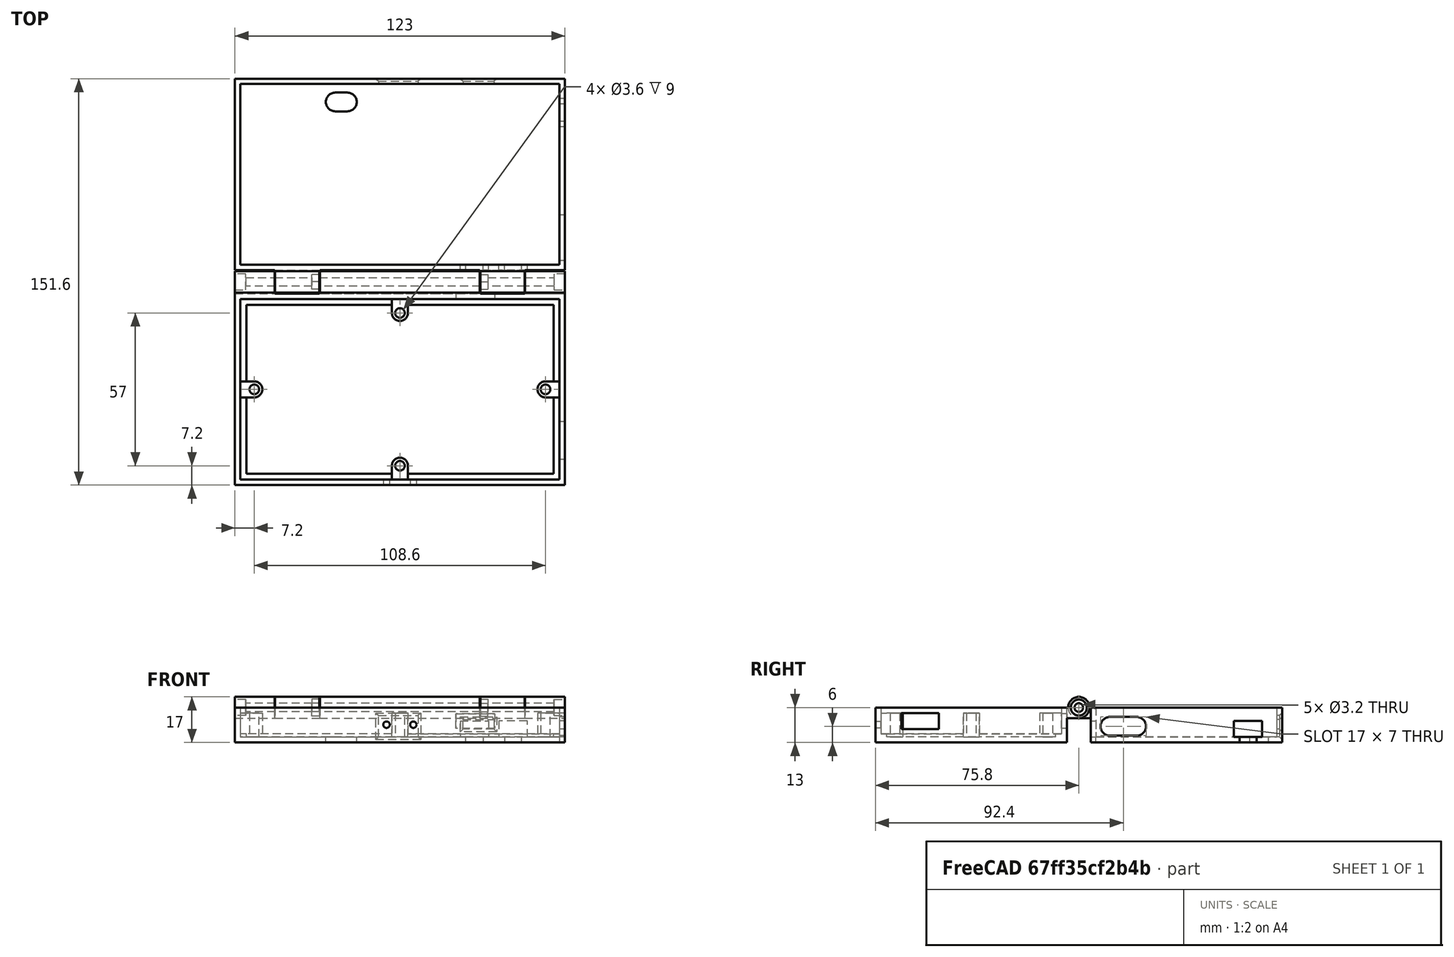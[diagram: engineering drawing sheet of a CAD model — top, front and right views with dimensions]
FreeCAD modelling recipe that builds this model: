
FCSTD DOCUMENT  (FreeCAD 1.0R39319 (Git))
Label: M3-MOD
License: All rights reserved
LicenseURL: http://en.wikipedia.org/wiki/All_rights_reserved
objects: Sketcher::SketchObject×31, PartDesign::Pocket×19, PartDesign::SubShapeBinder×12, PartDesign::Body×3, PartDesign::Pad×3, Mesh::Feature×2, PartDesign::Chamfer×1
note: 146 computed .brp shape members not serialized (recipe doc carries the construction recipe); baked Part::Feature solids carry a one-line shape summary decoded from their .brp

FEATURE [Sketcher::SketchObject] Sketch  label="Workspace"
  ArcFitTolerance = 0
  AttachmentSupport = -> [XY_Plane]
  FullyConstrained = true
  MakeInternals = false
  MapMode = 5
  sketch-geometry (24):
    g0: LineSegment StartX=-59.3 StartY=-6.6 StartZ=0 EndX=59.3 EndY=-6.6 EndZ=0
    g1: LineSegment StartX=59.3 StartY=-6.6 StartZ=0 EndX=59.3 EndY=-73.6 EndZ=0
    g2: LineSegment StartX=59.3 StartY=-73.6 StartZ=0 EndX=-59.3 EndY=-73.6 EndZ=0
    g3: LineSegment StartX=-59.3 StartY=-73.6 StartZ=0 EndX=-59.3 EndY=-6.6 EndZ=0
    g4: LineSegment StartX=-59.3 StartY=73.6 StartZ=0 EndX=59.3 EndY=73.6 EndZ=0
    g5: LineSegment StartX=59.3 StartY=73.6 StartZ=0 EndX=59.3 EndY=6.6 EndZ=0
    g6: LineSegment StartX=59.3 StartY=6.6 StartZ=0 EndX=-59.3 EndY=6.6 EndZ=0
    g7: LineSegment StartX=-59.3 StartY=6.6 StartZ=0 EndX=-59.3 EndY=73.6 EndZ=0
    g8: LineSegment StartX=-61.5 StartY=4 StartZ=0 EndX=-61.5 EndY=-4 EndZ=0
    g9: LineSegment StartX=-61.5 StartY=-4 StartZ=0 EndX=-46.5 EndY=-4 EndZ=0
    g10: LineSegment StartX=-46.5 StartY=-4 StartZ=0 EndX=-46.5 EndY=4 EndZ=0
    g11: LineSegment StartX=-46.5 StartY=4 StartZ=0 EndX=-61.5 EndY=4 EndZ=0
    g12: LineSegment StartX=-30 StartY=4 StartZ=0 EndX=-30 EndY=-4 EndZ=0
    g13: LineSegment StartX=-30 StartY=-4 StartZ=0 EndX=30 EndY=-4 EndZ=0
    g14: LineSegment StartX=30 StartY=-4 StartZ=0 EndX=30 EndY=4 EndZ=0
    g15: LineSegment StartX=30 StartY=4 StartZ=0 EndX=-30 EndY=4 EndZ=0
    g16: LineSegment StartX=61.5 StartY=4 StartZ=0 EndX=46.5 EndY=4 EndZ=0
    g17: LineSegment StartX=46.5 StartY=4 StartZ=0 EndX=46.5 EndY=-4 EndZ=0
    g18: LineSegment StartX=46.5 StartY=-4 StartZ=0 EndX=61.5 EndY=-4 EndZ=0
    g19: LineSegment StartX=61.5 StartY=-4 StartZ=0 EndX=61.5 EndY=4 EndZ=0
    g20: LineSegment StartX=-61.5 StartY=75.8 StartZ=0 EndX=-61.5 EndY=-75.8 EndZ=0
    g21: LineSegment StartX=-61.5 StartY=-75.8 StartZ=0 EndX=61.5 EndY=-75.8 EndZ=0
    g22: LineSegment StartX=61.5 StartY=-75.8 StartZ=0 EndX=61.5 EndY=75.8 EndZ=0
    g23: LineSegment StartX=61.5 StartY=75.8 StartZ=0 EndX=-61.5 EndY=75.8 EndZ=0
  constraints (68):
    c: Coincident(g0,g1)
    c: Coincident(g1,g2)
    c: Coincident(g2,g3)
    c: Coincident(g3,g0)
    c: Horizontal(g2)
    c: Vertical(g1)
    c: Vertical(g3)
    c: Symmetric(g0,g0,g-2)
    c: DistanceY(g1,g1) = 67
    c: DistanceY(g0,g-1) = 6.6
    c: Coincident(g4,g5)
    c: Coincident(g5,g6)
    c: Coincident(g6,g7)
    c: Coincident(g7,g4)
    c: Horizontal(g6)
    c: Vertical(g5)
    c: Vertical(g7)
    c: Equal(g0,g6)
    c: Equal(g1,g5)
    c: DistanceX(g2,g2) = 118.6
    c: DistanceY(g-1,g5) = 6.6
    c: Symmetric(g4,g4,g-2)
    c: Coincident(g8,g9)
    c: Coincident(g9,g10)
    c: Coincident(g10,g11)
    c: Coincident(g11,g8)
    c: Vertical(g10)
    c: Horizontal(g9)
    c: Horizontal(g11)
    c: Coincident(g12,g13)
    c: Coincident(g13,g14)
    c: Coincident(g14,g15)
    c: Coincident(g15,g12)
    c: Vertical(g12)
    c: Vertical(g14)
    c: Horizontal(g13)
    c: Coincident(g16,g17)
    c: Coincident(g17,g18)
    c: Coincident(g18,g19)
    c: Coincident(g19,g16)
    c: Horizontal(g16)
    c: Horizontal(g18)
    c: Vertical(g17)
    c: Vertical(g19)
    c: Coincident(g20,g21)
    c: Coincident(g21,g22)
    c: Coincident(g22,g23)
    c: Coincident(g23,g20)
    c: Vertical(g20)
    c: Vertical(g22)
    c: Horizontal(g21)
    c: Horizontal(g23)
    c: DistanceX(g20,g2) = 2.2
    c: DistanceX(g1,g21) = 2.2
    c: DistanceY(g20,g2) = 2.2
    c: DistanceY(g4,g20) = 2.2
    c: Equal(g10,g14)
    c: Equal(g14,g17)
    c: DistanceY(g19,g19) = 8
    c: Symmetric(g8,g8,g-1)
    c: Horizontal(g10,g12)
    c: Horizontal(g16,g14)
    c: Symmetric(g12,g14,g-2)
    c: Vertical(g20,g8)
    c: Vertical(g16,g22)
    c: Equal(g11,g16)
    c: DistanceX(g9,g9) = 15
    c: DistanceX(g13,g13) = 60
FEATURE [Sketcher::SketchObject] Sketch022  label="Key & SD"
  ArcFitTolerance = 0
  AttachmentOffset = pos=(0,0,-75.2) rot=(0,0,1;0rad)
  AttachmentSupport = -> [XZ_Plane]
  FullyConstrained = true
  MakeInternals = false
  MapMode = 5
  Placement = pos=(0,75.2,-1.67e-14) rot=(1,0,0;1.5708rad)
  sketch-geometry (8):
    g0: LineSegment StartX=23.5 StartY=-4.5 StartZ=0 EndX=35.1 EndY=-4.5 EndZ=0
    g1: LineSegment StartX=35.1 StartY=-4.5 StartZ=0 EndX=35.1 EndY=-8 EndZ=0
    g2: LineSegment StartX=35.1 StartY=-8 StartZ=0 EndX=23.5 EndY=-8 EndZ=0
    g3: LineSegment StartX=23.5 StartY=-8 StartZ=0 EndX=23.5 EndY=-4.5 EndZ=0
    g4: LineSegment StartX=-8 StartY=-3 StartZ=0 EndX=6.8 EndY=-3 EndZ=0
    g5: LineSegment StartX=6.8 StartY=-3 StartZ=0 EndX=6.8 EndY=-11 EndZ=0
    g6: LineSegment StartX=6.8 StartY=-11 StartZ=0 EndX=-8 EndY=-11 EndZ=0
    g7: LineSegment StartX=-8 StartY=-11 StartZ=0 EndX=-8 EndY=-3 EndZ=0
  constraints (24):
    c: Coincident(g0,g1)
    c: Coincident(g1,g2)
    c: Coincident(g2,g3)
    c: Coincident(g3,g0)
    c: Horizontal(g0)
    c: Horizontal(g2)
    c: Vertical(g1)
    c: Vertical(g3)
    c: Coincident(g4,g5)
    c: Coincident(g5,g6)
    c: Coincident(g6,g7)
    c: Coincident(g7,g4)
    c: Horizontal(g4)
    c: Horizontal(g6)
    c: Vertical(g5)
    c: Vertical(g7)
    c: DistanceX(g0,g0) = 11.6
    c: DistanceX(g4,g4) = 14.8
    c: DistanceY(g7,g7) = 8
    c: DistanceY(g1,g1) = 3.5
    c: DistanceX(g-1,g1) = 35.1
    c: DistanceX(g-1,g5) = 6.8
    c: DistanceY(g1,g-1) = 8
    c: DistanceY(g6,g-1) = 11
FEATURE [Sketcher::SketchObject] Sketch023  label="USB & CONN"
  ArcFitTolerance = 0
  AttachmentOffset = pos=(0,0,61.5) rot=(0,0,1;0rad)
  AttachmentSupport = -> [YZ_Plane]
  ExternalGeometry = -> [Sketch]
  FullyConstrained = true
  MakeInternals = false
  MapMode = 5
  Placement = pos=(61.5,0,0) rot=(0.57735,0.57735,0.57735;2.0944rad)
  sketch-geometry (12):
    g0: ArcOfCircle CenterX=11.6 CenterY=-7 CenterZ=0 NormalX=0 NormalY=0 NormalZ=1 AngleXU=0 Radius=3.5 StartAngle=1.5708 EndAngle=4.71239
    g1: ArcOfCircle CenterX=21.6 CenterY=-7 CenterZ=0 NormalX=0 NormalY=0 NormalZ=1 AngleXU=0 Radius=3.5 StartAngle=4.71239 EndAngle=7.85398
    g2: LineSegment StartX=11.6 StartY=-10.5 StartZ=0 EndX=21.6 EndY=-10.5 EndZ=0
    g3: LineSegment StartX=11.6 StartY=-3.5 StartZ=0 EndX=21.6 EndY=-3.5 EndZ=0
    g4: LineSegment StartX=57.8 StartY=-5 StartZ=0 EndX=68.4 EndY=-5 EndZ=0
    g5: LineSegment StartX=68.4 StartY=-5 StartZ=0 EndX=68.4 EndY=-11 EndZ=0
    g6: LineSegment StartX=68.4 StartY=-11 StartZ=0 EndX=66.3 EndY=-11 EndZ=0
    g7: LineSegment StartX=57.8 StartY=-11 StartZ=0 EndX=57.8 EndY=-5 EndZ=0
    g8: LineSegment StartX=66.3 StartY=-11 StartZ=0 EndX=66.3 EndY=-13 EndZ=0
    g9: LineSegment StartX=66.3 StartY=-13 StartZ=0 EndX=59.9 EndY=-13 EndZ=0
    g10: LineSegment StartX=59.9 StartY=-13 StartZ=0 EndX=59.9 EndY=-11 EndZ=0
    g11: LineSegment StartX=59.9 StartY=-11 StartZ=0 EndX=57.8 EndY=-11 EndZ=0
  constraints (33):
    c: Tangent(g0,g3) = 1.5708
    c: Tangent(g0,g2) = -1.5708
    c: Tangent(g2,g1) = -1.5708
    c: Tangent(g3,g1) = 1.5708
    c: Horizontal(g2)
    c: Equal(g0,g1)
    c: Coincident(g4,g5)
    c: Coincident(g5,g6)
    c: Coincident(g11,g7)
    c: Coincident(g7,g4)
    c: Horizontal(g4)
    c: Horizontal(g6)
    c: Vertical(g5)
    c: Vertical(g7)
    c: Coincident(g8,g9)
    c: Coincident(g9,g10)
    c: Horizontal(g9)
    c: Vertical(g8)
    c: Vertical(g10)
    c: Coincident(g6,g8)
    c: Coincident(g11,g10)
    c: Tangent(g6,g11)
    c: Equal(g6,g11)
    c: DistanceX(g9,g9) = 6.4
    c: DistanceX(g4,g4) = 10.6
    c: DistanceY(g5,g5) = 6
    c: DistanceY(g8,g5) = 2
    c: Radius(g1) = 3.5
    c: DistanceX(g0,g1) = 10
    c: DistanceY(g8,g-3) = 13
    c: DistanceX(g4,g-3) = 5.2
    c: DistanceY(g0,g-3) = 7
    c: DistanceX(g-3,g0) = 5
FEATURE [Sketcher::SketchObject] Sketch024  label="CONN 2"
  ArcFitTolerance = 0
  AttachmentOffset = pos=(0,0,-4.2) rot=(0,0,1;0rad)
  AttachmentSupport = -> [XZ_Plane]
  ExternalGeometry = -> [Sketch]
  FullyConstrained = true
  MakeInternals = false
  MapMode = 5
  Placement = pos=(0,4.2,-9e-16) rot=(1,0,0;1.5708rad)
  sketch-geometry (16):
    g0: LineSegment StartX=22.5 StartY=-5 StartZ=0 EndX=33.1 EndY=-5 EndZ=0
    g1: LineSegment StartX=33.1 StartY=-5 StartZ=0 EndX=33.1 EndY=-11 EndZ=0
    g2: LineSegment StartX=33.1 StartY=-11 StartZ=0 EndX=31 EndY=-11 EndZ=0
    g3: LineSegment StartX=22.5 StartY=-11 StartZ=0 EndX=22.5 EndY=-5 EndZ=0
    g4: LineSegment StartX=31 StartY=-11 StartZ=0 EndX=31 EndY=-13 EndZ=0
    g5: LineSegment StartX=31 StartY=-13 StartZ=0 EndX=24.6 EndY=-13 EndZ=0
    g6: LineSegment StartX=24.6 StartY=-13 StartZ=0 EndX=24.6 EndY=-11 EndZ=0
    g7: LineSegment StartX=36.9 StartY=-5 StartZ=0 EndX=47.5 EndY=-5 EndZ=0
    g8: LineSegment StartX=47.5 StartY=-5 StartZ=0 EndX=47.5 EndY=-11 EndZ=0
    g9: LineSegment StartX=47.5 StartY=-11 StartZ=0 EndX=45.4 EndY=-11 EndZ=0
    g10: LineSegment StartX=36.9 StartY=-11 StartZ=0 EndX=36.9 EndY=-5 EndZ=0
    g11: LineSegment StartX=45.4 StartY=-11 StartZ=0 EndX=45.4 EndY=-13 EndZ=0
    g12: LineSegment StartX=45.4 StartY=-13 StartZ=0 EndX=39 EndY=-13 EndZ=0
    g13: LineSegment StartX=39 StartY=-13 StartZ=0 EndX=39 EndY=-11 EndZ=0
    g14: LineSegment StartX=24.6 StartY=-11 StartZ=0 EndX=22.5 EndY=-11 EndZ=0
    g15: LineSegment StartX=39 StartY=-11 StartZ=0 EndX=36.9 EndY=-11 EndZ=0
  constraints (46):
    c: Coincident(g0,g1)
    c: Coincident(g1,g2)
    c: Coincident(g14,g3)
    c: Coincident(g3,g0)
    c: Horizontal(g0)
    c: Horizontal(g2)
    c: Vertical(g1)
    c: Vertical(g3)
    c: Coincident(g4,g5)
    c: Coincident(g5,g6)
    c: Horizontal(g5)
    c: Vertical(g4)
    c: Vertical(g6)
    c: Coincident(g7,g8)
    c: Coincident(g8,g9)
    c: Coincident(g15,g10)
    c: Coincident(g10,g7)
    c: Horizontal(g7)
    c: Horizontal(g9)
    c: Vertical(g8)
    c: Vertical(g10)
    c: Coincident(g11,g12)
    c: Coincident(g12,g13)
    c: Horizontal(g12)
    c: Vertical(g11)
    c: Vertical(g13)
    c: Coincident(g2,g4)
    c: Coincident(g14,g6)
    c: Tangent(g2,g14)
    c: Coincident(g9,g11)
    c: Coincident(g15,g13)
    c: Tangent(g9,g15)
    c: Equal(g14,g2)
    c: Equal(g2,g15)
    c: Equal(g15,g9)
    c: Equal(g1,g10)
    c: Equal(g0,g7)
    c: Horizontal(g4,g12)
    c: Horizontal(g1,g10)
    c: DistanceY(g11,g8) = 2
    c: DistanceX(g7,g7) = 10.6
    c: DistanceY(g8,g8) = 6
    c: DistanceX(g12,g12) = 6.4
    c: DistanceY(g11,g-1) = 13
    c: DistanceX(g7,g-3) = 11.8
    c: DistanceX(g0,g-3) = 26.2
FEATURE [Sketcher::SketchObject] Sketch025  label="RESET"
  ArcFitTolerance = 0
  AttachmentSupport = -> [XY_Plane]
  ExternalGeometry = -> [Sketch]
  FullyConstrained = true
  MakeInternals = false
  MapMode = 5
  sketch-geometry (4):
    g0: ArcOfCircle CenterX=-24.1 CenterY=67.1 CenterZ=0 NormalX=0 NormalY=0 NormalZ=1 AngleXU=0 Radius=3.5 StartAngle=1.5708 EndAngle=4.71239
    g1: ArcOfCircle CenterX=-19.6 CenterY=67.1 CenterZ=0 NormalX=0 NormalY=0 NormalZ=1 AngleXU=0 Radius=3.5 StartAngle=4.71239 EndAngle=7.85398
    g2: LineSegment StartX=-24.1 StartY=63.6 StartZ=0 EndX=-19.6 EndY=63.6 EndZ=0
    g3: LineSegment StartX=-24.1 StartY=70.6 StartZ=0 EndX=-19.6 EndY=70.6 EndZ=0
  constraints (10):
    c: Tangent(g0,g3) = 1.5708
    c: Tangent(g0,g2) = -1.5708
    c: Tangent(g2,g1) = -1.5708
    c: Tangent(g3,g1) = 1.5708
    c: Horizontal(g2)
    c: Equal(g0,g1)
    c: Radius(g0) = 3.5
    c: DistanceX(g0,g1) = 4.5
    c: DistanceX(g-3,g0) = 35.2
    c: DistanceY(g0,g-4) = 3
FEATURE [Sketcher::SketchObject] Sketch031  label="FIX HOLE"
  ArcFitTolerance = 0
  AttachmentSupport = -> [XY_Plane]
  ExternalGeometry = -> [Sketch]
  FullyConstrained = true
  MakeInternals = false
  MapMode = 5
  sketch-geometry (32):
    g0: LineSegment StartX=-3 StartY=-8.6 StartZ=0 EndX=3 EndY=-8.6 EndZ=0
    g1: LineSegment StartX=3 StartY=-8.6 StartZ=0 EndX=3 EndY=-11.6 EndZ=0
    g2: LineSegment StartX=2.02025e-10 StartY=-14.6 StartZ=0 EndX=-2.01994e-10 EndY=-14.6 EndZ=0
    g3: LineSegment StartX=-3 StartY=-11.6 StartZ=0 EndX=-3 EndY=-8.6 EndZ=0
    g4: LineSegment StartX=54.3 StartY=-37.1 StartZ=0 EndX=57.3 EndY=-37.1 EndZ=0
    g5: LineSegment StartX=57.3 StartY=-37.1 StartZ=0 EndX=57.3 EndY=-43.1 EndZ=0
    g6: LineSegment StartX=57.3 StartY=-43.1 StartZ=0 EndX=54.3 EndY=-43.1 EndZ=0
    g7: LineSegment StartX=51.3 StartY=-40.1 StartZ=0 EndX=51.3 EndY=-40.1 EndZ=0
    g8: LineSegment StartX=-2.04292e-10 StartY=-65.6 StartZ=0 EndX=2.04323e-10 EndY=-65.6 EndZ=0
    g9: LineSegment StartX=3 StartY=-68.6 StartZ=0 EndX=3 EndY=-71.6 EndZ=0
    g10: LineSegment StartX=3 StartY=-71.6 StartZ=0 EndX=-3 EndY=-71.6 EndZ=0
    g11: LineSegment StartX=-3 StartY=-71.6 StartZ=0 EndX=-3 EndY=-68.6 EndZ=0
    g12: LineSegment StartX=-57.3 StartY=-37.1 StartZ=0 EndX=-54.3 EndY=-37.1 EndZ=0
    g13: LineSegment StartX=-51.3 StartY=-40.1 StartZ=0 EndX=-51.3 EndY=-40.1 EndZ=0
    g14: LineSegment StartX=-54.3 StartY=-43.1 StartZ=0 EndX=-57.3 EndY=-43.1 EndZ=0
    g15: LineSegment StartX=-57.3 StartY=-43.1 StartZ=0 EndX=-57.3 EndY=-37.1 EndZ=0
    g16: ArcOfCircle CenterX=-54.3 CenterY=-40.1 CenterZ=0 NormalX=0 NormalY=0 NormalZ=1 AngleXU=0 Radius=3 StartAngle=5.39571e-11 EndAngle=1.5708
    g17: ArcOfCircle CenterX=-54.3 CenterY=-40.1 CenterZ=0 NormalX=0 NormalY=0 NormalZ=1 AngleXU=0 Radius=3 StartAngle=4.71239 EndAngle=6.28319
    g18: ArcOfCircle CenterX=-4.11221e-11 CenterY=-11.6 CenterZ=0 NormalX=0 NormalY=0 NormalZ=1 AngleXU=0 Radius=3 StartAngle=3.14159 EndAngle=4.71239
    g19: ArcOfCircle CenterX=4.12844e-11 CenterY=-11.6 CenterZ=0 NormalX=0 NormalY=0 NormalZ=1 AngleXU=0 Radius=3 StartAngle=4.71239 EndAngle=6.28319
    g20: ArcOfCircle CenterX=-4.0526e-11 CenterY=-68.6 CenterZ=0 NormalX=0 NormalY=0 NormalZ=1 AngleXU=0 Radius=3 StartAngle=1.5708 EndAngle=3.14159
    g21: ArcOfCircle CenterX=4.0686e-11 CenterY=-68.6 CenterZ=0 NormalX=0 NormalY=0 NormalZ=1 AngleXU=0 Radius=3 StartAngle=5.62494e-11 EndAngle=1.5708
    g22: ArcOfCircle CenterX=54.3 CenterY=-40.1 CenterZ=0 NormalX=0 NormalY=0 NormalZ=1 AngleXU=0 Radius=3 StartAngle=1.5708 EndAngle=3.14159
    g23: ArcOfCircle CenterX=54.3 CenterY=-40.1 CenterZ=0 NormalX=0 NormalY=0 NormalZ=1 AngleXU=0 Radius=3 StartAngle=3.14159 EndAngle=4.71239
    g24: LineSegment [constr] StartX=57.3 StartY=-8.6 StartZ=0 EndX=57.3 EndY=-37.1 EndZ=0
    g25: LineSegment [constr] StartX=57.3 StartY=-71.6 StartZ=0 EndX=57.3 EndY=-43.1 EndZ=0
    g26: LineSegment [constr] StartX=-57.3 StartY=-71.6 StartZ=0 EndX=-3 EndY=-71.6 EndZ=0
    g27: LineSegment [constr] StartX=3 StartY=-71.6 StartZ=0 EndX=57.3 EndY=-71.6 EndZ=0
    g28: LineSegment [constr] StartX=-57.3 StartY=-71.6 StartZ=0 EndX=-57.3 EndY=-43.1 EndZ=0
    g29: LineSegment [constr] StartX=-57.3 StartY=-37.1 StartZ=0 EndX=-57.3 EndY=-8.6 EndZ=0
    g30: LineSegment [constr] StartX=-57.3 StartY=-8.6 StartZ=0 EndX=-3 EndY=-8.6 EndZ=0
    g31: LineSegment [constr] StartX=3 StartY=-8.6 StartZ=0 EndX=57.3 EndY=-8.6 EndZ=0
  constraints (84):
    c: Coincident(g0,g1)
    c: Coincident(g3,g0)
    c: Horizontal(g0)
    c: Horizontal(g2)
    c: Vertical(g1)
    c: Vertical(g3)
    c: Coincident(g4,g5)
    c: Coincident(g5,g6)
    c: Horizontal(g4)
    c: Horizontal(g6)
    c: Vertical(g5)
    c: Vertical(g7)
    c: Coincident(g9,g10)
    c: Coincident(g10,g11)
    c: Horizontal(g8)
    c: Horizontal(g10)
    c: Vertical(g9)
    c: Vertical(g11)
    c: Coincident(g14,g15)
    c: Coincident(g15,g12)
    c: Horizontal(g12)
    c: Horizontal(g14)
    c: Vertical(g13)
    c: Vertical(g15)
    c: Tangent(g12,g16) = 1.5708
    c: Tangent(g13,g16) = 1.5708
    c: Tangent(g13,g17) = 1.5708
    c: Tangent(g14,g17) = 1.5708
    c: Tangent(g2,g18) = 1.5708
    c: Tangent(g3,g18) = 1.5708
    c: Tangent(g1,g19) = 1.5708
    c: Tangent(g2,g19) = 1.5708
    c: Tangent(g8,g20) = 1.5708
    c: Tangent(g11,g20) = 1.5708
    c: Tangent(g8,g21) = 1.5708
    c: Tangent(g9,g21) = 1.5708
    c: Tangent(g4,g22) = 1.5708
    c: Tangent(g7,g22) = 1.5708
    c: Tangent(g6,g23) = 1.5708
    c: Tangent(g7,g23) = 1.5708
    c: Equal(g16,g17)
    c: Equal(g17,g18)
    c: Equal(g18,g19)
    c: Equal(g19,g20)
    c: Equal(g20,g21)
    c: Equal(g21,g23)
    c: Equal(g23,g22)
    c: Equal(g0,g5)
    c: Equal(g5,g10)
    c: Equal(g10,g15)
    c: Equal(g12,g1)
    c: Equal(g1,g6)
    c: Equal(g6,g11)
    c: DistanceX(g10,g10) = 6
    c: DistanceX(g25,g-5) = 2
    c: DistanceY(g-5,g25) = 2
    c: Coincident(g24,g4)
    c: Vertical(g24)
    c: Coincident(g25,g5)
    c: Vertical(g25)
    c: Equal(g24,g25)
    c: DistanceX(g-3,g29) = 2
    c: DistanceY(g29,g-3) = 2
    c: Coincident(g26,g10)
    c: Horizontal(g26)
    c: Coincident(g27,g9)
    c: Coincident(g27,g25)
    c: Horizontal(g27)
    c: Coincident(g28,g26)
    c: Coincident(g28,g14)
    c: Coincident(g29,g12)
    c: Coincident(g30,g29)
    c: Coincident(g30,g0)
    c: Coincident(g31,g0)
    c: Coincident(g31,g24)
    c: Horizontal(g31)
    c: Horizontal(g30)
    c: Vertical(g29)
    c: Vertical(g28)
    c: Equal(g28,g29)
    c: Equal(g30,g31)
    c: Equal(g26,g27)
    c: Radius(g21) = 3
    c: DistanceY(g9,g9) = 3
FEATURE [Sketcher::SketchObject] Sketch032  label="PARTS"
  ArcFitTolerance = 0
  AttachmentSupport = -> [XY_Plane]
  ExternalGeometry = -> [Sketch]
  FullyConstrained = true
  MakeInternals = false
  MapMode = 5
  sketch-geometry (44):
    g0: LineSegment StartX=6.9 StartY=-59.2 StartZ=0 EndX=22.3 EndY=-59.2 EndZ=0
    g1: LineSegment StartX=22.3 StartY=-59.2 StartZ=0 EndX=22.3 EndY=-71.2 EndZ=0
    g2: LineSegment StartX=22.3 StartY=-71.2 StartZ=0 EndX=6.9 EndY=-71.2 EndZ=0
    g3: LineSegment StartX=6.9 StartY=-71.2 StartZ=0 EndX=6.9 EndY=-59.2 EndZ=0
    g4: LineSegment StartX=-56.3 StartY=-9.4 StartZ=0 EndX=-36.3 EndY=-9.4 EndZ=0
    g5: LineSegment StartX=-36.3 StartY=-9.4 StartZ=0 EndX=-36.3 EndY=-23.4 EndZ=0
    g6: LineSegment StartX=-36.3 StartY=-23.4 StartZ=0 EndX=-56.3 EndY=-23.4 EndZ=0
    g7: LineSegment StartX=-56.3 StartY=-23.4 StartZ=0 EndX=-56.3 EndY=-9.4 EndZ=0
    g8: LineSegment StartX=-58.1 StartY=-46.6 StartZ=0 EndX=-32.1 EndY=-46.6 EndZ=0
    g9: LineSegment StartX=-32.1 StartY=-46.6 StartZ=0 EndX=-32.1 EndY=-72.6 EndZ=0
    g10: LineSegment StartX=-32.1 StartY=-72.6 StartZ=0 EndX=-58.1 EndY=-72.6 EndZ=0
    g11: LineSegment StartX=-58.1 StartY=-72.6 StartZ=0 EndX=-58.1 EndY=-46.6 EndZ=0
    g12: LineSegment StartX=43.9 StartY=-8.5 StartZ=0 EndX=58.9 EndY=-8.5 EndZ=0
    g13: LineSegment StartX=58.9 StartY=-8.5 StartZ=0 EndX=58.9 EndY=-32 EndZ=0
    g14: LineSegment StartX=58.9 StartY=-32 StartZ=0 EndX=43.9 EndY=-32 EndZ=0
    g15: LineSegment StartX=43.9 StartY=-32 StartZ=0 EndX=43.9 EndY=-8.5 EndZ=0
    g16: LineSegment StartX=24.3 StartY=-47.2 StartZ=0 EndX=58.3 EndY=-47.2 EndZ=0
    g17: LineSegment StartX=58.3 StartY=-47.2 StartZ=0 EndX=58.3 EndY=-72.6 EndZ=0
    g18: LineSegment StartX=58.3 StartY=-72.6 StartZ=0 EndX=24.3 EndY=-72.6 EndZ=0
    g19: LineSegment StartX=24.3 StartY=-72.6 StartZ=0 EndX=24.3 EndY=-47.2 EndZ=0
    g20: LineSegment StartX=-59.3 StartY=-6.6 StartZ=0 EndX=59.3 EndY=-6.6 EndZ=0
    g21: LineSegment StartX=59.3 StartY=-6.6 StartZ=0 EndX=59.3 EndY=-73.6 EndZ=0
    g22: LineSegment StartX=59.3 StartY=-73.6 StartZ=0 EndX=-59.3 EndY=-73.6 EndZ=0
    g23: LineSegment StartX=-59.3 StartY=-73.6 StartZ=0 EndX=-59.3 EndY=-6.6 EndZ=0
    g24: LineSegment StartX=21.9 StartY=-10.6 StartZ=0 EndX=34.3 EndY=-10.6 EndZ=0
    g25: LineSegment StartX=34.3 StartY=-10.6 StartZ=0 EndX=34.3 EndY=-18.6 EndZ=0
    g26: LineSegment StartX=34.3 StartY=-18.6 StartZ=0 EndX=21.9 EndY=-18.6 EndZ=0
    g27: LineSegment StartX=21.9 StartY=-18.6 StartZ=0 EndX=21.9 EndY=-10.6 EndZ=0
    g28: LineSegment StartX=2.2 StartY=-22.9 StartZ=0 EndX=-2.2 EndY=-22.9 EndZ=0
    g29: LineSegment StartX=-2.2 StartY=-22.9 StartZ=0 EndX=-2.2 EndY=-27.3 EndZ=0
    g30: LineSegment StartX=-2.2 StartY=-27.3 StartZ=0 EndX=2.2 EndY=-27.3 EndZ=0
    g31: LineSegment StartX=2.2 StartY=-27.3 StartZ=0 EndX=2.2 EndY=-22.9 EndZ=0
    g32: LineSegment StartX=-14.9 StartY=-35.6 StartZ=0 EndX=-10.5 EndY=-35.6 EndZ=0
    g33: LineSegment StartX=-10.5 StartY=-35.6 StartZ=0 EndX=-10.5 EndY=-40 EndZ=0
    g34: LineSegment StartX=-10.5 StartY=-40 StartZ=0 EndX=-14.9 EndY=-40 EndZ=0
    g35: LineSegment StartX=-14.9 StartY=-40 StartZ=0 EndX=-14.9 EndY=-35.6 EndZ=0
    g36: LineSegment StartX=10.5 StartY=-35.6 StartZ=0 EndX=14.9 EndY=-35.6 EndZ=0
    g37: LineSegment StartX=14.9 StartY=-35.6 StartZ=0 EndX=14.9 EndY=-40 EndZ=0
    g38: LineSegment StartX=14.9 StartY=-40 StartZ=0 EndX=10.5 EndY=-40 EndZ=0
    g39: LineSegment StartX=10.5 StartY=-40 StartZ=0 EndX=10.5 EndY=-35.6 EndZ=0
    g40: LineSegment StartX=-2.2 StartY=-48.7 StartZ=0 EndX=2.2 EndY=-48.7 EndZ=0
    g41: LineSegment StartX=2.2 StartY=-48.7 StartZ=0 EndX=2.2 EndY=-53.1 EndZ=0
    g42: LineSegment StartX=2.2 StartY=-53.1 StartZ=0 EndX=-2.2 EndY=-53.1 EndZ=0
    g43: LineSegment StartX=-2.2 StartY=-53.1 StartZ=0 EndX=-2.2 EndY=-48.7 EndZ=0
  constraints (128):
    c: Coincident(g0,g1)
    c: Coincident(g1,g2)
    c: Coincident(g2,g3)
    c: Coincident(g3,g0)
    c: Horizontal(g0)
    c: Horizontal(g2)
    c: Vertical(g1)
    c: Vertical(g3)
    c: Coincident(g4,g5)
    c: Coincident(g5,g6)
    c: Coincident(g6,g7)
    c: Coincident(g7,g4)
    c: Horizontal(g4)
    c: Horizontal(g6)
    c: Vertical(g5)
    c: Vertical(g7)
    c: Coincident(g8,g9)
    c: Coincident(g9,g10)
    c: Coincident(g10,g11)
    c: Coincident(g11,g8)
    c: Horizontal(g8)
    c: Horizontal(g10)
    c: Vertical(g9)
    c: Vertical(g11)
    c: Coincident(g12,g13)
    c: Coincident(g13,g14)
    c: Coincident(g14,g15)
    c: Coincident(g15,g12)
    c: Horizontal(g12)
    c: Horizontal(g14)
    c: Vertical(g13)
    c: Vertical(g15)
    c: Coincident(g16,g17)
    c: Coincident(g18,g19)
    c: Coincident(g19,g16)
    c: Horizontal(g16)
    c: Horizontal(g18)
    c: Vertical(g17)
    c: Vertical(g19)
    c: Coincident(g20,g21)
    c: Coincident(g21,g22)
    c: Coincident(g22,g23)
    c: Coincident(g23,g20)
    c: Horizontal(g20)
    c: Horizontal(g22)
    c: Vertical(g21)
    c: Vertical(g23)
    c: DistanceY(g18,g17) = 25.4
    c: DistanceX(g18,g18) = 34
    c: Equal(g10,g11)
    c: DistanceX(g10,g10) = 26
    c: DistanceY(g13,g13) = 23.5
    c: DistanceX(g12,g12) = 15
    c: DistanceX(g4,g4) = 20
    c: DistanceY(g7,g7) = 14
    c: DistanceY(g3,g3) = 12
    c: Coincident(g20,g-3)
    c: Coincident(g21,g-4)
    c: Coincident(g17,g18)
    c: DistanceX(g2,g2) = 15.4
    c: Coincident(g24,g25)
    c: Coincident(g25,g26)
    c: Coincident(g26,g27)
    c: Coincident(g27,g24)
    c: Horizontal(g24)
    c: Horizontal(g26)
    c: Vertical(g25)
    c: Vertical(g27)
    c: DistanceX(g26,g26) = 12.4
    c: DistanceY(g27,g27) = 8
    c: DistanceY(g4,g20) = 2.8
    c: DistanceX(g20,g4) = 3
    c: DistanceX(g22,g10) = 1.2
    c: DistanceY(g22,g10) = 1
    c: DistanceY(g21,g17) = 1
    c: DistanceX(g17,g21) = 1
    c: DistanceY(g21,g1) = 2.4
    c: DistanceX(g1,g21) = 37
    c: DistanceX(g12,g20) = 0.4
    c: DistanceY(g12,g20) = 1.9
    c: DistanceX(g24,g20) = 25
    c: DistanceY(g24,g20) = 4
    c: Coincident(g28,g29)
    c: Coincident(g29,g30)
    c: Coincident(g30,g31)
    c: Coincident(g31,g28)
    c: Horizontal(g30)
    c: Vertical(g29)
    c: Vertical(g31)
    c: Coincident(g32,g33)
    c: Coincident(g33,g34)
    c: Coincident(g34,g35)
    c: Coincident(g35,g32)
    c: Horizontal(g32)
    c: Horizontal(g34)
    c: Vertical(g33)
    c: Vertical(g35)
    c: Coincident(g36,g37)
    c: Coincident(g37,g38)
    c: Coincident(g38,g39)
    c: Coincident(g39,g36)
    c: Horizontal(g36)
    c: Horizontal(g38)
    c: Vertical(g37)
    c: Vertical(g39)
    c: Coincident(g40,g41)
    c: Coincident(g41,g42)
    c: Coincident(g42,g43)
    c: Coincident(g43,g40)
    c: Horizontal(g40)
    c: Horizontal(g42)
    c: Vertical(g41)
    c: Vertical(g43)
    c: Equal(g35,g32)
    c: Equal(g32,g31)
    c: Equal(g31,g28)
    c: Equal(g28,g39)
    c: Equal(g39,g36)
    c: Equal(g36,g43)
    c: Equal(g43,g40)
    c: DistanceY(g37,g37) = 4.4
    c: Symmetric(g32,g36,g-2)
    c: Vertical(g40,g30)
    c: Symmetric(g28,g28,g-2)
    c: DistanceX(g33,g38) = 21
    c: DistanceY(g40,g29) = 21.4
    c: DistanceY(g32,g20) = 29
    c: DistanceY(g28,g20) = 16.3
FEATURE [Sketcher::SketchObject] Sketch033  label="BODY-DISP"
  ArcFitTolerance = 0
  AttachmentSupport = -> [YZ_Plane]
  FullyConstrained = true
  MakeInternals = false
  MapMode = 5
  Placement = pos=(0,0,0) rot=(0.57735,0.57735,0.57735;2.0944rad)
  sketch-geometry (8):
    g0: Circle CenterX=0 CenterY=0 CenterZ=0 NormalX=0 NormalY=0 NormalZ=1 AngleXU=0 Radius=1.6
    g1: ArcOfCircle CenterX=0 CenterY=0 CenterZ=0 NormalX=0 NormalY=0 NormalZ=1 AngleXU=0 Radius=4 StartAngle=0 EndAngle=4.71239
    g2: LineSegment StartX=4 StartY=0 StartZ=0 EndX=4.4 EndY=0 EndZ=0
    g3: LineSegment StartX=4.4 StartY=0 StartZ=0 EndX=75.8 EndY=0 EndZ=0
    g4: LineSegment StartX=75.8 StartY=0 StartZ=0 EndX=75.8 EndY=-13 EndZ=0
    g5: LineSegment StartX=75.8 StartY=-13 StartZ=0 EndX=4.4 EndY=-13 EndZ=0
    g6: LineSegment StartX=4.4 StartY=-13 StartZ=0 EndX=4.4 EndY=-4 EndZ=0
    g7: LineSegment StartX=4.4 StartY=-4 StartZ=0 EndX=0 EndY=-4 EndZ=0
  constraints (23):
    c: Coincident(g0,g-1)
    c: Coincident(g1,g0)
    c: Horizontal(g0,g1)
    c: Radius(g0) = 1.6
    c: Radius(g1) = 4
    c: Coincident(g2,g1)
    c: PointOnObject(g2,g-1)
    c: Coincident(g3,g2)
    c: PointOnObject(g3,g-1)
    c: Coincident(g4,g3)
    c: Vertical(g4)
    c: Coincident(g5,g4)
    c: Horizontal(g5)
    c: Coincident(g6,g5)
    c: Vertical(g2,g5)
    c: DistanceX(g5,g5) = 71.4
    c: DistanceX(g2,g2) = 0.4
    c: DistanceY(g4,g4) = 13
    c: Coincident(g7,g6)
    c: Vertical(g6)
    c: Vertical(g0,g1)
    c: Coincident(g7,g1)
    c: Horizontal(g7)
FEATURE [Sketcher::SketchObject] Sketch034  label="BODY-MAIN"
  ArcFitTolerance = 0
  AttachmentSupport = -> [YZ_Plane]
  FullyConstrained = true
  MakeInternals = false
  MapMode = 5
  Placement = pos=(0,0,0) rot=(0.57735,0.57735,0.57735;2.0944rad)
  sketch-geometry (8):
    g0: Circle CenterX=0 CenterY=0 CenterZ=0 NormalX=0 NormalY=0 NormalZ=1 AngleXU=0 Radius=1.6
    g1: ArcOfCircle CenterX=0 CenterY=0 CenterZ=0 NormalX=0 NormalY=0 NormalZ=1 AngleXU=0 Radius=4 StartAngle=4.71239 EndAngle=9.42478
    g2: LineSegment StartX=-4 StartY=1.5e-15 StartZ=0 EndX=-4.4 EndY=1.5e-15 EndZ=0
    g3: LineSegment StartX=-4.4 StartY=1.5e-15 StartZ=0 EndX=-75.8 EndY=0 EndZ=0
    g4: LineSegment StartX=-75.8 StartY=0 StartZ=0 EndX=-75.8 EndY=-13 EndZ=0
    g5: LineSegment StartX=-75.8 StartY=-13 StartZ=0 EndX=-4.4 EndY=-13 EndZ=0
    g6: LineSegment StartX=-4.4 StartY=-13 StartZ=0 EndX=-4.4 EndY=-4 EndZ=0
    g7: LineSegment StartX=0 StartY=-4 StartZ=0 EndX=-4.4 EndY=-4 EndZ=0
  constraints (23):
    c: Coincident(g0,g-1)
    c: Coincident(g1,g0)
    c: Coincident(g2,g1)
    c: PointOnObject(g2,g-1)
    c: Horizontal(g2)
    c: Coincident(g3,g2)
    c: PointOnObject(g3,g-1)
    c: Coincident(g4,g3)
    c: Vertical(g4)
    c: Coincident(g5,g4)
    c: Horizontal(g5)
    c: Coincident(g6,g5)
    c: Radius(g0) = 1.6
    c: Radius(g1) = 4
    c: Vertical(g2,g5)
    c: DistanceX(g5,g5) = 71.4
    c: DistanceX(g2,g1) = 0.4
    c: DistanceY(g4,g4) = 13
    c: Vertical(g0,g1)
    c: Vertical(g2,g6)
    c: Coincident(g7,g1)
    c: Coincident(g7,g6)
    c: Horizontal(g7)
FEATURE [PartDesign::Body] Body
  AllowCompound = false
  Group = -> [Sketch033,Sketch034,Sketch,Sketch022,Sketch023,Sketch024,Sketch025,Sketch031,Sketch032]
  Origin = -> Origin
FEATURE [PartDesign::SubShapeBinder] Binder
  BindCopyOnChange = 0
  BindMode = 0
  ClaimChildren = false
  Context = -> Body001 [Binder.]
  Fuse = false
  MakeFace = true
  OffsetFill = false
  OffsetIntersection = false
  OffsetJoinType = 0
  OffsetOpenResult = false
  PartialLoad = false
  Refine = true
  Relative = true
  Support = -> [Body[Sketch033.Edge1,Sketch033.Edge2,Sketch033.Edge3,Sketch033.Edge4,Sketch033.Edge5,Sketch033.Edge7,Sketch033.Edge6,Sketch033.Edge8]]
  _Version = 2
FEATURE [Sketcher::SketchObject] Sketch035
  ArcFitTolerance = 1e-06
  AttachmentSupport = -> [Binder]
  ExternalGeometry = -> [Binder]
  FullyConstrained = true
  MakeInternals = false
  MapMode = 5
  Placement = pos=(0,0,0) rot=(0.57735,0.57735,0.57735;2.0944rad)
  sketch-geometry (7):
    g0: Circle CenterX=0 CenterY=0 CenterZ=0 NormalX=0 NormalY=0 NormalZ=1 AngleXU=0 Radius=1.6
    g1: ArcOfCircle CenterX=0 CenterY=0 CenterZ=0 NormalX=0 NormalY=0 NormalZ=1 AngleXU=0 Radius=4 StartAngle=0 EndAngle=4.71238
    g2: LineSegment StartX=-2.60969e-05 StartY=-4 StartZ=0 EndX=4.4 EndY=-4 EndZ=0
    g3: LineSegment StartX=4.4 StartY=-4 StartZ=0 EndX=4.4 EndY=-13 EndZ=0
    g4: LineSegment StartX=4.4 StartY=-13 StartZ=0 EndX=75.8 EndY=-13 EndZ=0
    g5: LineSegment StartX=75.8 StartY=-13 StartZ=0 EndX=75.8 EndY=0 EndZ=0
    g6: LineSegment StartX=75.8 StartY=0 StartZ=0 EndX=4 EndY=0 EndZ=0
  constraints (15):
    c: Coincident(g0,g-1)
    c: Coincident(g1,g0)
    c: Coincident(g1,g-3)
    c: Coincident(g2,g1)
    c: Coincident(g2,g-4)
    c: Horizontal(g2)
    c: Coincident(g3,g2)
    c: Coincident(g3,g-4)
    c: Coincident(g4,g3)
    c: Coincident(g4,g-5)
    c: Coincident(g5,g4)
    c: Coincident(g5,g-5)
    c: Coincident(g6,g5)
    c: Coincident(g6,g1)
    c: PointOnObject(g-6,g0)
FEATURE [PartDesign::Pad] Pad
  Direction = (1,0,0)
  Length = 61.5
  Length2 = 61.5
  Profile = -> Sketch035
  ReferenceAxis = -> Sketch035 [N_Axis]
  Refine = true
  Suppressed = false
  Type = 4
FEATURE [PartDesign::SubShapeBinder] Binder001
  BindCopyOnChange = 0
  BindMode = 0
  ClaimChildren = false
  Context = -> Body002 [Binder001.]
  Fuse = false
  MakeFace = true
  OffsetFill = false
  OffsetIntersection = false
  OffsetJoinType = 0
  OffsetOpenResult = false
  PartialLoad = false
  Refine = true
  Relative = true
  Support = -> [Body[Sketch034.Edge4,Sketch034.Edge5,Sketch034.Edge6,Sketch034.Edge7,Sketch034.Edge8,Sketch034.Edge2,Sketch034.Edge3,Sketch034.Edge1]]
  _Version = 2
FEATURE [Sketcher::SketchObject] Sketch036
  ArcFitTolerance = 1e-06
  AttachmentSupport = -> [Binder001]
  ExternalGeometry = -> [Binder001]
  FullyConstrained = true
  MakeInternals = false
  MapMode = 5
  Placement = pos=(0,0,0) rot=(0.57735,0.57735,0.57735;2.0944rad)
  sketch-geometry (7):
    g0: Circle CenterX=0 CenterY=0 CenterZ=0 NormalX=0 NormalY=0 NormalZ=1 AngleXU=0 Radius=1.6
    g1: ArcOfCircle CenterX=0 CenterY=0 CenterZ=0 NormalX=0 NormalY=0 NormalZ=1 AngleXU=0 Radius=4 StartAngle=4.71239 EndAngle=9.42478
    g2: LineSegment StartX=-7e-16 StartY=-4 StartZ=0 EndX=-4.4 EndY=-4 EndZ=0
    g3: LineSegment StartX=-4.4 StartY=-4 StartZ=0 EndX=-4.4 EndY=-13 EndZ=0
    g4: LineSegment StartX=-4.4 StartY=-13 StartZ=0 EndX=-75.8 EndY=-13 EndZ=0
    g5: LineSegment StartX=-75.8 StartY=-13 StartZ=0 EndX=-75.8 EndY=0 EndZ=0
    g6: LineSegment StartX=-75.8 StartY=0 StartZ=0 EndX=-4 EndY=1.5e-15 EndZ=0
  constraints (15):
    c: Coincident(g-1,g0)
    c: Coincident(g1,g0)
    c: Coincident(g1,g-5)
    c: Coincident(g1,g-5)
    c: Coincident(g2,g1)
    c: Coincident(g2,g-4)
    c: Coincident(g3,g2)
    c: Coincident(g3,g-4)
    c: Coincident(g4,g3)
    c: Coincident(g4,g-3)
    c: Coincident(g5,g4)
    c: Coincident(g5,g-3)
    c: Coincident(g6,g5)
    c: Coincident(g6,g1)
    c: Equal(g0,g-6)
FEATURE [PartDesign::Pad] Pad001
  Direction = (1,0,0)
  Length = 61.5
  Length2 = 61.5
  Profile = -> Sketch036
  ReferenceAxis = -> Sketch036 [N_Axis]
  Refine = true
  Suppressed = false
  Type = 4
FEATURE [PartDesign::SubShapeBinder] Binder002
  BindCopyOnChange = 0
  BindMode = 0
  ClaimChildren = false
  Context = -> Body002 [Binder002.]
  Fuse = false
  MakeFace = true
  OffsetFill = false
  OffsetIntersection = false
  OffsetJoinType = 0
  OffsetOpenResult = false
  PartialLoad = false
  Refine = true
  Relative = true
  Support = -> [Body[Sketch.Edge9,Sketch.Edge10,Sketch.Edge12,Sketch.Edge11,Sketch.Edge13,Sketch.Edge14,Sketch.Edge16,Sketch.Edge15]]
  _Version = 2
FEATURE [Sketcher::SketchObject] Sketch037
  ArcFitTolerance = 1e-06
  AttachmentSupport = -> [XY_Plane002]
  ExternalGeometry = -> [Binder002]
  FullyConstrained = true
  MakeInternals = false
  MapMode = 5
  sketch-geometry (8):
    g0: LineSegment StartX=-46.5 StartY=4 StartZ=0 EndX=-46.5 EndY=-4 EndZ=0
    g1: LineSegment StartX=-46.5 StartY=-4 StartZ=0 EndX=-30 EndY=-4 EndZ=0
    g2: LineSegment StartX=-30 StartY=-4 StartZ=0 EndX=-30 EndY=4 EndZ=0
    g3: LineSegment StartX=-30 StartY=4 StartZ=0 EndX=-46.5 EndY=4 EndZ=0
    g4: LineSegment StartX=30 StartY=4 StartZ=0 EndX=30 EndY=-4 EndZ=0
    g5: LineSegment StartX=30 StartY=-4 StartZ=0 EndX=46.5 EndY=-4 EndZ=0
    g6: LineSegment StartX=46.5 StartY=-4 StartZ=0 EndX=46.5 EndY=4 EndZ=0
    g7: LineSegment StartX=46.5 StartY=4 StartZ=0 EndX=30 EndY=4 EndZ=0
  constraints (20):
    c: Coincident(g0,g1)
    c: Coincident(g1,g2)
    c: Coincident(g2,g3)
    c: Coincident(g3,g0)
    c: Vertical(g0)
    c: Vertical(g2)
    c: Horizontal(g1)
    c: Horizontal(g3)
    c: Coincident(g0,g-3)
    c: Coincident(g1,g-4)
    c: Coincident(g4,g5)
    c: Coincident(g5,g6)
    c: Coincident(g6,g7)
    c: Coincident(g7,g4)
    c: Vertical(g4)
    c: Vertical(g6)
    c: Horizontal(g5)
    c: Horizontal(g7)
    c: Coincident(g4,g-5)
    c: Coincident(g5,g-6)
FEATURE [PartDesign::Pocket] Pocket
  BaseFeature = -> Pad001
  Direction = (0,0,-1)
  Length = 4
  Length2 = 4
  Profile = -> Sketch037
  ReferenceAxis = -> Sketch037 [N_Axis]
  Refine = true
  Suppressed = false
  Type = 4
FEATURE [PartDesign::SubShapeBinder] Binder003
  BindCopyOnChange = 0
  BindMode = 0
  ClaimChildren = false
  Context = -> Body001 [Binder003.]
  Fuse = false
  MakeFace = true
  OffsetFill = false
  OffsetIntersection = false
  OffsetJoinType = 0
  OffsetOpenResult = false
  PartialLoad = false
  Refine = true
  Relative = true
  Support = -> [Body[Sketch.Edge11,Sketch.Edge10,Sketch.Edge12,Sketch.Edge13,Sketch.Edge16,Sketch.Edge14,Sketch.Edge15,Sketch.Edge18]]
  _Version = 2
FEATURE [Sketcher::SketchObject] Sketch038
  ArcFitTolerance = 1e-06
  AttachmentSupport = -> [XY_Plane001]
  ExternalGeometry = -> [Binder003]
  FullyConstrained = true
  MakeInternals = false
  MapMode = 5
  sketch-geometry (12):
    g0: LineSegment StartX=-61.5 StartY=4 StartZ=0 EndX=-61.5 EndY=-4 EndZ=0
    g1: LineSegment StartX=-61.5 StartY=-4 StartZ=0 EndX=-46.7 EndY=-4 EndZ=0
    g2: LineSegment StartX=-46.7 StartY=-4 StartZ=0 EndX=-46.7 EndY=4 EndZ=0
    g3: LineSegment StartX=-46.7 StartY=4 StartZ=0 EndX=-61.5 EndY=4 EndZ=0
    g4: LineSegment StartX=-29.8 StartY=4 StartZ=0 EndX=-29.8 EndY=-4 EndZ=0
    g5: LineSegment StartX=-29.8 StartY=-4 StartZ=0 EndX=29.8 EndY=-4 EndZ=0
    g6: LineSegment StartX=29.8 StartY=-4 StartZ=0 EndX=29.8 EndY=4 EndZ=0
    g7: LineSegment StartX=29.8 StartY=4 StartZ=0 EndX=-29.8 EndY=4 EndZ=0
    g8: LineSegment StartX=61.5 StartY=4 StartZ=0 EndX=46.7 EndY=4 EndZ=0
    g9: LineSegment StartX=46.7 StartY=4 StartZ=0 EndX=46.7 EndY=-4 EndZ=0
    g10: LineSegment StartX=46.7 StartY=-4 StartZ=0 EndX=61.5 EndY=-4 EndZ=0
    g11: LineSegment StartX=61.5 StartY=-4 StartZ=0 EndX=61.5 EndY=4 EndZ=0
  constraints (32):
    c: Coincident(g0,g1)
    c: Coincident(g1,g2)
    c: Coincident(g2,g3)
    c: Coincident(g3,g0)
    c: Vertical(g2)
    c: Horizontal(g1)
    c: Horizontal(g3)
    c: Coincident(g4,g5)
    c: Coincident(g5,g6)
    c: Coincident(g6,g7)
    c: Coincident(g7,g4)
    c: Vertical(g4)
    c: Vertical(g6)
    c: Horizontal(g5)
    c: Horizontal(g7)
    c: Coincident(g8,g9)
    c: Coincident(g9,g10)
    c: Coincident(g10,g11)
    c: Coincident(g11,g8)
    c: Horizontal(g8)
    c: Horizontal(g10)
    c: Vertical(g9)
    c: Coincident(g0,g-3)
    c: Coincident(g0,g-4)
    c: Coincident(g-7,g8)
    c: Coincident(g-8,g10)
    c: Horizontal(g-6,g4)
    c: Horizontal(g-5,g4)
    c: DistanceX(g2,g-3) = 0.2
    c: DistanceX(g-6,g4) = 0.2
    c: DistanceX(g6,g-6) = 0.2
    c: DistanceX(g-7,g8) = 0.2
FEATURE [PartDesign::Pocket] Pocket001
  BaseFeature = -> Pad
  Direction = (0,0,-1)
  Length = 4
  Length2 = 4
  Profile = -> Sketch038
  ReferenceAxis = -> Sketch038 [N_Axis]
  Refine = true
  Suppressed = false
  Type = 4
FEATURE [PartDesign::SubShapeBinder] Binder004
  BindCopyOnChange = 0
  BindMode = 0
  ClaimChildren = false
  Context = -> Body001 [Binder004.]
  Fuse = false
  MakeFace = true
  OffsetFill = false
  OffsetIntersection = false
  OffsetJoinType = 0
  OffsetOpenResult = false
  PartialLoad = false
  Refine = true
  Relative = true
  Support = -> [Body[Sketch.Edge8,Sketch.Edge7,Sketch.Edge5,Sketch.Edge6]]
  _Version = 2
FEATURE [Sketcher::SketchObject] Sketch039
  ArcFitTolerance = 1e-06
  AttachmentSupport = -> [XY_Plane001]
  ExternalGeometry = -> [Binder004]
  FullyConstrained = true
  MakeInternals = false
  MapMode = 5
  sketch-geometry (4):
    g0: LineSegment StartX=-59.5 StartY=73.8 StartZ=0 EndX=-59.5 EndY=6.4 EndZ=0
    g1: LineSegment StartX=-59.5 StartY=6.4 StartZ=0 EndX=59.5 EndY=6.4 EndZ=0
    g2: LineSegment StartX=59.5 StartY=6.4 StartZ=0 EndX=59.5 EndY=73.8 EndZ=0
    g3: LineSegment StartX=59.5 StartY=73.8 StartZ=0 EndX=-59.5 EndY=73.8 EndZ=0
  constraints (12):
    c: Coincident(g0,g1)
    c: Coincident(g1,g2)
    c: Coincident(g2,g3)
    c: Coincident(g3,g0)
    c: Vertical(g0)
    c: Vertical(g2)
    c: Horizontal(g1)
    c: Horizontal(g3)
    c: DistanceX(g0,g-3) = 0.2
    c: DistanceY(g-3,g0) = 0.2
    c: DistanceX(g-4,g1) = 0.2
    c: DistanceY(g1,g-4) = 0.2
FEATURE [PartDesign::Pocket] Pocket002
  BaseFeature = -> Pocket001
  Direction = (0,0,-1)
  Length = 11
  Length2 = 5
  Profile = -> Sketch039
  ReferenceAxis = -> Sketch039 [N_Axis]
  Refine = true
  Suppressed = false
  Type = 0
FEATURE [PartDesign::SubShapeBinder] Binder005
  BindCopyOnChange = 0
  BindMode = 0
  ClaimChildren = false
  Context = -> Body001 [Binder005.]
  Fuse = false
  MakeFace = true
  OffsetFill = false
  OffsetIntersection = false
  OffsetJoinType = 0
  OffsetOpenResult = false
  PartialLoad = false
  Refine = true
  Relative = true
  Support = -> [Body[Sketch025.Edge3,Sketch025.Edge1,Sketch025.Edge4,Sketch025.Edge2]]
  _Version = 2
FEATURE [PartDesign::SubShapeBinder] Binder006
  BindCopyOnChange = 0
  BindMode = 0
  ClaimChildren = false
  Context = -> Body001 [Binder006.]
  Fuse = false
  MakeFace = true
  OffsetFill = false
  OffsetIntersection = false
  OffsetJoinType = 0
  OffsetOpenResult = false
  PartialLoad = false
  Refine = true
  Relative = true
  Support = -> [Body[Sketch022.Edge8,Sketch022.Edge5,Sketch022.Edge6,Sketch022.Edge7,Sketch022.Edge4,Sketch022.Edge1,Sketch022.Edge3,Sketch022.Edge2]]
  _Version = 2
FEATURE [PartDesign::SubShapeBinder] Binder007
  BindCopyOnChange = 0
  BindMode = 0
  ClaimChildren = false
  Context = -> Body001 [Binder007.]
  Fuse = false
  MakeFace = true
  OffsetFill = false
  OffsetIntersection = false
  OffsetJoinType = 0
  OffsetOpenResult = false
  PartialLoad = false
  Refine = true
  Relative = true
  Support = -> [Body[Sketch024.Edge8,Sketch024.Edge1,Sketch024.Edge2,Sketch024.Edge3,Sketch024.Edge4,Sketch024.Edge5,Sketch024.Edge6,Sketch024.Edge7]]
  _Version = 2
FEATURE [PartDesign::SubShapeBinder] Binder008
  BindCopyOnChange = 0
  BindMode = 0
  ClaimChildren = false
  Context = -> Body001 [Binder008.]
  Fuse = false
  MakeFace = true
  OffsetFill = false
  OffsetIntersection = false
  OffsetJoinType = 0
  OffsetOpenResult = false
  PartialLoad = false
  Refine = true
  Relative = true
  Support = -> [Body[Sketch023.]]
  _Version = 2
FEATURE [Sketcher::SketchObject] Sketch040
  ArcFitTolerance = 1e-06
  AttachmentSupport = -> [XY_Plane001]
  ExternalGeometry = -> [Binder005]
  FullyConstrained = true
  MakeInternals = false
  MapMode = 5
  sketch-geometry (4):
    g0: ArcOfCircle CenterX=-24.1 CenterY=67.1 CenterZ=0 NormalX=0 NormalY=0 NormalZ=1 AngleXU=0 Radius=3.5 StartAngle=1.5708 EndAngle=4.71239
    g1: ArcOfCircle CenterX=-19.6 CenterY=67.1 CenterZ=0 NormalX=0 NormalY=0 NormalZ=1 AngleXU=0 Radius=3.5 StartAngle=4.71239 EndAngle=7.85398
    g2: LineSegment StartX=-24.1 StartY=70.6 StartZ=0 EndX=-19.6 EndY=70.6 EndZ=0
    g3: LineSegment StartX=-24.1 StartY=63.6 StartZ=0 EndX=-19.6 EndY=63.6 EndZ=0
  constraints (10):
    c: Coincident(g3,g0)
    c: Coincident(g3,g1)
    c: Coincident(g2,g0)
    c: Coincident(g1,g2)
    c: Coincident(g-3,g0)
    c: Coincident(g0,g-3)
    c: Coincident(g-3,g0)
    c: Coincident(g1,g-4)
    c: Coincident(g1,g-4)
    c: Coincident(g1,g-4)
FEATURE [PartDesign::Pocket] Pocket003
  BaseFeature = -> Pocket002
  Direction = (0,0,-1)
  Length = 5
  Length2 = 5
  Profile = -> Sketch040
  ReferenceAxis = -> Sketch040 [N_Axis]
  Refine = true
  Suppressed = false
  Type = 1
FEATURE [Sketcher::SketchObject] Sketch041
  ArcFitTolerance = 1e-06
  AttachmentSupport = -> [Pocket003]
  ExternalGeometry = -> [Binder006]
  FullyConstrained = true
  MakeInternals = false
  MapMode = 5
  Placement = pos=(0,75.8,0) rot=(0,0.707107,0.707107;3.14159rad)
  sketch-geometry (8):
    g0: LineSegment StartX=-35.1 StartY=-4.5 StartZ=0 EndX=-35.1 EndY=-8 EndZ=0
    g1: LineSegment StartX=-35.1 StartY=-8 StartZ=0 EndX=-23.5 EndY=-8 EndZ=0
    g2: LineSegment StartX=-23.5 StartY=-8 StartZ=0 EndX=-23.5 EndY=-4.5 EndZ=0
    g3: LineSegment StartX=-23.5 StartY=-4.5 StartZ=0 EndX=-35.1 EndY=-4.5 EndZ=0
    g4: LineSegment StartX=-6.8 StartY=-3 StartZ=0 EndX=-6.8 EndY=-11 EndZ=0
    g5: LineSegment StartX=-6.8 StartY=-11 StartZ=0 EndX=8 EndY=-11 EndZ=0
    g6: LineSegment StartX=8 StartY=-11 StartZ=0 EndX=8 EndY=-3 EndZ=0
    g7: LineSegment StartX=8 StartY=-3 StartZ=0 EndX=-6.8 EndY=-3 EndZ=0
  constraints (20):
    c: Coincident(g0,g1)
    c: Coincident(g1,g2)
    c: Coincident(g2,g3)
    c: Coincident(g3,g0)
    c: Vertical(g0)
    c: Vertical(g2)
    c: Horizontal(g1)
    c: Horizontal(g3)
    c: Coincident(g0,g-3)
    c: Coincident(g1,g-4)
    c: Coincident(g4,g5)
    c: Coincident(g5,g6)
    c: Coincident(g6,g7)
    c: Coincident(g7,g4)
    c: Vertical(g4)
    c: Vertical(g6)
    c: Horizontal(g5)
    c: Horizontal(g7)
    c: Coincident(g4,g-5)
    c: Coincident(g5,g-6)
FEATURE [PartDesign::Pocket] Pocket004
  BaseFeature = -> Pocket003
  Direction = (0,-1,2e-16)
  Length = 2
  Length2 = 5
  Profile = -> Sketch041
  ReferenceAxis = -> Sketch041 [N_Axis]
  Refine = true
  Suppressed = false
  Type = 0
FEATURE [Sketcher::SketchObject] Sketch042
  ArcFitTolerance = 1e-06
  AttachmentSupport = -> [Pocket004]
  ExternalGeometry = -> [Binder007]
  FullyConstrained = true
  MakeInternals = false
  MapMode = 5
  Placement = pos=(0,4.4,0) rot=(1,0,0;1.5708rad)
  sketch-geometry (16):
    g0: LineSegment StartX=22.5 StartY=-5 StartZ=0 EndX=33.1 EndY=-5 EndZ=0
    g1: LineSegment StartX=33.1 StartY=-5 StartZ=0 EndX=33.1 EndY=-11 EndZ=0
    g2: LineSegment StartX=33.1 StartY=-11 StartZ=0 EndX=31 EndY=-11 EndZ=0
    g3: LineSegment StartX=31 StartY=-11 StartZ=0 EndX=31 EndY=-13 EndZ=0
    g4: LineSegment StartX=31 StartY=-13 StartZ=0 EndX=24.6 EndY=-13 EndZ=0
    g5: LineSegment StartX=24.6 StartY=-13 StartZ=0 EndX=24.6 EndY=-11 EndZ=0
    g6: LineSegment StartX=24.6 StartY=-11 StartZ=0 EndX=22.5 EndY=-11 EndZ=0
    g7: LineSegment StartX=22.5 StartY=-5 StartZ=0 EndX=22.5 EndY=-11 EndZ=0
    g8: LineSegment StartX=36.9 StartY=-5 StartZ=0 EndX=36.9 EndY=-11 EndZ=0
    g9: LineSegment StartX=36.9 StartY=-11 StartZ=0 EndX=39 EndY=-11 EndZ=0
    g10: LineSegment StartX=39 StartY=-11 StartZ=0 EndX=39 EndY=-13 EndZ=0
    g11: LineSegment StartX=39 StartY=-13 StartZ=0 EndX=45.4 EndY=-13 EndZ=0
    g12: LineSegment StartX=45.4 StartY=-13 StartZ=0 EndX=45.4 EndY=-11 EndZ=0
    g13: LineSegment StartX=45.4 StartY=-11 StartZ=0 EndX=47.5 EndY=-11 EndZ=0
    g14: LineSegment StartX=47.5 StartY=-11 StartZ=0 EndX=47.5 EndY=-5 EndZ=0
    g15: LineSegment StartX=47.5 StartY=-5 StartZ=0 EndX=36.9 EndY=-5 EndZ=0
  constraints (32):
    c: Coincident(g0,g-3)
    c: Coincident(g0,g-4)
    c: Coincident(g1,g0)
    c: Coincident(g1,g-4)
    c: Coincident(g2,g1)
    c: Coincident(g2,g-5)
    c: Coincident(g3,g2)
    c: Coincident(g3,g-5)
    c: Coincident(g4,g3)
    c: Coincident(g4,g-6)
    c: Coincident(g5,g4)
    c: Coincident(g5,g-6)
    c: Coincident(g6,g5)
    c: Coincident(g6,g-3)
    c: Coincident(g7,g0)
    c: Coincident(g7,g6)
    c: Coincident(g8,g-7)
    c: Coincident(g8,g-7)
    c: Coincident(g9,g8)
    c: Coincident(g9,g-8)
    c: Coincident(g10,g9)
    c: Coincident(g10,g-8)
    c: Coincident(g11,g10)
    c: Coincident(g11,g-9)
    c: Coincident(g12,g11)
    c: Coincident(g12,g-9)
    c: Coincident(g13,g12)
    c: Coincident(g13,g-10)
    c: Coincident(g14,g13)
    c: Coincident(g14,g-10)
    c: Coincident(g15,g14)
    c: Coincident(g15,g8)
FEATURE [PartDesign::Pocket] Pocket005
  BaseFeature = -> Pocket004
  Direction = (0,1,-2e-16)
  Length = 2
  Length2 = 5
  Profile = -> Sketch042
  ReferenceAxis = -> Sketch042 [N_Axis]
  Refine = true
  Suppressed = false
  Type = 0
FEATURE [Sketcher::SketchObject] Sketch043
  ArcFitTolerance = 1e-06
  AttachmentSupport = -> [Pocket005]
  ExternalGeometry = -> [Binder008]
  FullyConstrained = true
  MakeInternals = false
  MapMode = 5
  Placement = pos=(61.5,0,0) rot=(0.57735,0.57735,0.57735;2.0944rad)
  sketch-geometry (12):
    g0: LineSegment StartX=57.8 StartY=-5 StartZ=0 EndX=68.4 EndY=-5 EndZ=0
    g1: LineSegment StartX=68.4 StartY=-5 StartZ=0 EndX=68.4 EndY=-11 EndZ=0
    g2: LineSegment StartX=68.4 StartY=-11 StartZ=0 EndX=66.3 EndY=-11 EndZ=0
    g3: LineSegment StartX=66.3 StartY=-11 StartZ=0 EndX=66.3 EndY=-13 EndZ=0
    g4: LineSegment StartX=66.3 StartY=-13 StartZ=0 EndX=59.9 EndY=-13 EndZ=0
    g5: LineSegment StartX=59.9 StartY=-13 StartZ=0 EndX=59.9 EndY=-11 EndZ=0
    g6: LineSegment StartX=59.9 StartY=-11 StartZ=0 EndX=57.8 EndY=-11 EndZ=0
    g7: LineSegment StartX=57.8 StartY=-11 StartZ=0 EndX=57.8 EndY=-5 EndZ=0
    g8: LineSegment StartX=11.6 StartY=-3.5 StartZ=0 EndX=21.6 EndY=-3.5 EndZ=0
    g9: LineSegment StartX=21.6 StartY=-10.5 StartZ=0 EndX=11.6 EndY=-10.5 EndZ=0
    g10: ArcOfCircle CenterX=21.6 CenterY=-7 CenterZ=0 NormalX=0 NormalY=0 NormalZ=1 AngleXU=0 Radius=3.5 StartAngle=4.71239 EndAngle=7.85398
    g11: ArcOfCircle CenterX=11.6 CenterY=-7 CenterZ=0 NormalX=0 NormalY=0 NormalZ=1 AngleXU=0 Radius=3.5 StartAngle=1.5708 EndAngle=4.71239
  constraints (26):
    c: Coincident(g0,g-5)
    c: Coincident(g0,g-6)
    c: Coincident(g1,g0)
    c: Coincident(g1,g-6)
    c: Coincident(g2,g1)
    c: Coincident(g2,g-7)
    c: Coincident(g3,g2)
    c: Coincident(g3,g-7)
    c: Coincident(g4,g3)
    c: Coincident(g4,g-8)
    c: Coincident(g5,g4)
    c: Coincident(g5,g-8)
    c: Coincident(g6,g5)
    c: Coincident(g6,g-5)
    c: Coincident(g7,g6)
    c: Coincident(g7,g0)
    c: Coincident(g-3,g11)
    c: Coincident(g11,g-3)
    c: Coincident(g11,g-3)
    c: Coincident(g11,g8)
    c: Coincident(g9,g11)
    c: Coincident(g10,g-4)
    c: Coincident(g10,g-4)
    c: Coincident(g10,g-4)
    c: Coincident(g8,g10)
    c: Coincident(g9,g10)
FEATURE [PartDesign::Pocket] Pocket006
  BaseFeature = -> Pocket005
  Direction = (-1,0,0)
  Length = 2
  Length2 = 5
  Profile = -> Sketch043
  ReferenceAxis = -> Sketch043 [N_Axis]
  Refine = true
  Suppressed = false
  Type = 0
FEATURE [PartDesign::SubShapeBinder] Binder009
  BindCopyOnChange = 0
  BindMode = 0
  ClaimChildren = false
  Context = -> Body002 [Binder009.]
  Fuse = false
  MakeFace = true
  OffsetFill = false
  OffsetIntersection = false
  OffsetJoinType = 0
  OffsetOpenResult = false
  PartialLoad = false
  Refine = true
  Relative = true
  Support = -> [Body[Sketch.Edge21,Sketch.Edge23,Sketch.Edge22,Sketch.Edge3,Sketch.Edge4,Sketch.Edge2,Sketch.Edge1,Sketch.Edge10]]
  _Version = 2
FEATURE [PartDesign::SubShapeBinder] Binder010
  BindCopyOnChange = 0
  BindMode = 0
  ClaimChildren = false
  Context = -> Body002 [Binder010.]
  Fuse = false
  MakeFace = true
  OffsetFill = false
  OffsetIntersection = false
  OffsetJoinType = 0
  OffsetOpenResult = false
  PartialLoad = false
  Refine = true
  Relative = true
  Support = -> [Body[Sketch031.Edge17,Sketch031.Edge18,Sketch031.Edge19,Sketch031.Edge20,Sketch031.Edge16,Sketch031.Edge13,Sketch031.Edge12,Sketch031.Edge11]]
  _Version = 2
FEATURE [Sketcher::SketchObject] Sketch044
  ArcFitTolerance = 1e-06
  AttachmentSupport = -> [XY_Plane002]
  ExternalGeometry = -> [Binder009]
  FullyConstrained = true
  MakeInternals = false
  MapMode = 5
  sketch-geometry (4):
    g0: LineSegment StartX=-59.5 StartY=-6.4 StartZ=0 EndX=-59.5 EndY=-73.8 EndZ=0
    g1: LineSegment StartX=-59.5 StartY=-73.8 StartZ=0 EndX=59.5 EndY=-73.8 EndZ=0
    g2: LineSegment StartX=59.5 StartY=-73.8 StartZ=0 EndX=59.5 EndY=-6.4 EndZ=0
    g3: LineSegment StartX=59.5 StartY=-6.4 StartZ=0 EndX=-59.5 EndY=-6.4 EndZ=0
  constraints (12):
    c: Coincident(g0,g1)
    c: Coincident(g1,g2)
    c: Coincident(g2,g3)
    c: Coincident(g3,g0)
    c: Vertical(g0)
    c: Vertical(g2)
    c: Horizontal(g1)
    c: Horizontal(g3)
    c: DistanceX(g0,g-3) = 0.2
    c: DistanceY(g-3,g0) = 0.2
    c: DistanceX(g-4,g1) = 0.2
    c: DistanceY(g1,g-4) = 0.2
FEATURE [PartDesign::Pocket] Pocket007
  BaseFeature = -> Pocket
  Direction = (0,0,-1)
  Length = 2
  Length2 = 5
  Profile = -> Sketch044
  ReferenceAxis = -> Sketch044 [N_Axis]
  Refine = true
  Suppressed = false
  Type = 0
FEATURE [Sketcher::SketchObject] Sketch045
  ArcFitTolerance = 1e-06
  AttachmentSupport = -> [Pocket007]
  ExternalGeometry = -> [Binder009]
  FullyConstrained = true
  MakeInternals = false
  MapMode = 5
  Placement = pos=(0,0,-2) rot=(0,0,1;0rad)
  sketch-geometry (4):
    g0: LineSegment StartX=-57.3 StartY=-8.6 StartZ=0 EndX=-57.3 EndY=-71.6 EndZ=0
    g1: LineSegment StartX=-57.3 StartY=-71.6 StartZ=0 EndX=57.3 EndY=-71.6 EndZ=0
    g2: LineSegment StartX=57.3 StartY=-71.6 StartZ=0 EndX=57.3 EndY=-8.6 EndZ=0
    g3: LineSegment StartX=57.3 StartY=-8.6 StartZ=0 EndX=-57.3 EndY=-8.6 EndZ=0
  constraints (12):
    c: Coincident(g0,g1)
    c: Coincident(g1,g2)
    c: Coincident(g2,g3)
    c: Coincident(g3,g0)
    c: Vertical(g0)
    c: Vertical(g2)
    c: Horizontal(g1)
    c: Horizontal(g3)
    c: DistanceX(g-3,g0) = 2
    c: DistanceY(g0,g-3) = 2
    c: DistanceX(g1,g-4) = 2
    c: DistanceY(g-4,g1) = 2
FEATURE [PartDesign::Pocket] Pocket008
  BaseFeature = -> Pocket007
  Direction = (0,0,-1)
  Length = 9
  Length2 = 5
  Profile = -> Sketch045
  ReferenceAxis = -> Sketch045 [N_Axis]
  Refine = true
  Suppressed = false
  Type = 0
FEATURE [Sketcher::SketchObject] Sketch046
  ArcFitTolerance = 1e-06
  AttachmentSupport = -> [Pocket008]
  ExternalGeometry = -> [Binder010]
  FullyConstrained = true
  MakeInternals = false
  MapMode = 5
  Placement = pos=(0,0,-11) rot=(0,0,1;0rad)
  sketch-geometry (20):
    g0: ArcOfCircle CenterX=-54.3 CenterY=-40.1 CenterZ=0 NormalX=0 NormalY=0 NormalZ=1 AngleXU=0 Radius=3 StartAngle=4.71239 EndAngle=7.85398
    g1: LineSegment StartX=-54.3 StartY=-43.1 StartZ=0 EndX=-57.3 EndY=-43.1 EndZ=0
    g2: LineSegment StartX=-57.3 StartY=-43.1 StartZ=0 EndX=-57.3 EndY=-37.1 EndZ=0
    g3: LineSegment StartX=-57.3 StartY=-37.1 StartZ=0 EndX=-54.3 EndY=-37.1 EndZ=0
    g4: ArcOfCircle CenterX=-4.11221e-11 CenterY=-11.6 CenterZ=0 NormalX=0 NormalY=0 NormalZ=1 AngleXU=0 Radius=3 StartAngle=3.14159 EndAngle=6.28319
    g5: LineSegment StartX=-3 StartY=-11.6 StartZ=0 EndX=-3 EndY=-8.6 EndZ=0
    g6: LineSegment StartX=-3 StartY=-8.6 StartZ=0 EndX=3 EndY=-8.6 EndZ=0
    g7: LineSegment StartX=3 StartY=-8.6 StartZ=0 EndX=3 EndY=-11.6 EndZ=0
    g8: ArcOfCircle CenterX=54.3 CenterY=-40.1 CenterZ=0 NormalX=0 NormalY=0 NormalZ=1 AngleXU=0 Radius=3 StartAngle=1.5708 EndAngle=4.71239
    g9: LineSegment StartX=54.3 StartY=-37.1 StartZ=0 EndX=57.3 EndY=-37.1 EndZ=0
    g10: LineSegment StartX=57.3 StartY=-37.1 StartZ=0 EndX=57.3 EndY=-43.1 EndZ=0
    g11: LineSegment StartX=57.3 StartY=-43.1 StartZ=0 EndX=54.3 EndY=-43.1 EndZ=0
    g12: ArcOfCircle CenterX=4.0686e-11 CenterY=-68.6 CenterZ=0 NormalX=0 NormalY=0 NormalZ=1 AngleXU=0 Radius=3 StartAngle=5.62513e-11 EndAngle=3.14159
    g13: LineSegment StartX=-3 StartY=-68.6 StartZ=0 EndX=-3 EndY=-71.6 EndZ=0
    g14: LineSegment StartX=-3 StartY=-71.6 StartZ=0 EndX=3 EndY=-71.6 EndZ=0
    g15: LineSegment StartX=3 StartY=-71.6 StartZ=0 EndX=3 EndY=-68.6 EndZ=0
    g16: Circle CenterX=4.0686e-11 CenterY=-68.6 CenterZ=0 NormalX=0 NormalY=0 NormalZ=1 AngleXU=0 Radius=1.8
    g17: Circle CenterX=54.3 CenterY=-40.1 CenterZ=0 NormalX=0 NormalY=0 NormalZ=1 AngleXU=0 Radius=1.8
    g18: Circle CenterX=-4.11221e-11 CenterY=-11.6 CenterZ=0 NormalX=0 NormalY=0 NormalZ=1 AngleXU=0 Radius=1.8
    g19: Circle CenterX=-54.3 CenterY=-40.1 CenterZ=0 NormalX=0 NormalY=0 NormalZ=1 AngleXU=0 Radius=1.8
  constraints (44):
    c: Coincident(g0,g-4)
    c: Coincident(g0,g-4)
    c: Vertical(g0,g0)
    c: Coincident(g1,g0)
    c: Coincident(g1,g-3)
    c: Coincident(g2,g1)
    c: Coincident(g2,g-3)
    c: Coincident(g3,g2)
    c: Coincident(g3,g0)
    c: Coincident(g4,g-6)
    c: Coincident(g4,g-6)
    c: Horizontal(g4,g4)
    c: Coincident(g5,g4)
    c: Coincident(g5,g-5)
    c: Coincident(g6,g5)
    c: Coincident(g6,g-5)
    c: Coincident(g7,g6)
    c: Coincident(g7,g4)
    c: Coincident(g8,g-8)
    c: Coincident(g8,g-8)
    c: Vertical(g8,g8)
    c: Coincident(g9,g8)
    c: Coincident(g9,g-7)
    c: Coincident(g10,g9)
    c: Coincident(g10,g-7)
    c: Coincident(g11,g10)
    c: Coincident(g11,g8)
    c: Coincident(g12,g-10)
    c: Coincident(g12,g-10)
    c: Horizontal(g12,g12)
    c: Coincident(g13,g12)
    c: Coincident(g13,g-9)
    c: Coincident(g14,g13)
    c: Coincident(g14,g-9)
    c: Coincident(g15,g14)
    c: Coincident(g15,g12)
    c: Coincident(g16,g12)
    c: Coincident(g17,g8)
    c: Coincident(g18,g4)
    c: Coincident(g19,g0)
    c: Equal(g19,g18)
    c: Equal(g18,g17)
    c: Equal(g17,g16)
    c: Radius(g16) = 1.8
FEATURE [PartDesign::Pad] Pad002
  BaseFeature = -> Pocket008
  Direction = (0,0,1)
  Length = 9
  Length2 = 10
  Profile = -> Sketch046
  ReferenceAxis = -> Sketch046 [N_Axis]
  Refine = true
  Suppressed = false
  Type = 0
FEATURE [Sketcher::SketchObject] Sketch047
  ArcFitTolerance = 1e-06
  AttachmentSupport = -> [Pad002]
  ExternalGeometry = -> [Pad002]
  FullyConstrained = true
  MakeInternals = false
  MapMode = 5
  Placement = pos=(0,0,-2) rot=(0,0,1;0rad)
  sketch-geometry (16):
    g0: LineSegment StartX=-59.5 StartY=-6.4 StartZ=0 EndX=-59.5 EndY=-37.1 EndZ=0
    g1: LineSegment StartX=-59.5 StartY=-37.1 StartZ=0 EndX=-3 EndY=-37.1 EndZ=0
    g2: LineSegment StartX=-3 StartY=-37.1 StartZ=0 EndX=-3 EndY=-6.4 EndZ=0
    g3: LineSegment StartX=-3 StartY=-6.4 StartZ=0 EndX=-59.5 EndY=-6.4 EndZ=0
    g4: LineSegment StartX=59.5 StartY=-6.4 StartZ=0 EndX=3 EndY=-6.4 EndZ=0
    g5: LineSegment StartX=3 StartY=-6.4 StartZ=0 EndX=3 EndY=-37.1 EndZ=0
    g6: LineSegment StartX=3 StartY=-37.1 StartZ=0 EndX=59.5 EndY=-37.1 EndZ=0
    g7: LineSegment StartX=59.5 StartY=-37.1 StartZ=0 EndX=59.5 EndY=-6.4 EndZ=0
    g8: LineSegment StartX=59.5 StartY=-73.8 StartZ=0 EndX=59.5 EndY=-43.1 EndZ=0
    g9: LineSegment StartX=59.5 StartY=-43.1 StartZ=0 EndX=3 EndY=-43.1 EndZ=0
    g10: LineSegment StartX=3 StartY=-43.1 StartZ=0 EndX=3 EndY=-73.8 EndZ=0
    g11: LineSegment StartX=3 StartY=-73.8 StartZ=0 EndX=59.5 EndY=-73.8 EndZ=0
    g12: LineSegment StartX=-59.5 StartY=-73.8 StartZ=0 EndX=-3 EndY=-73.8 EndZ=0
    g13: LineSegment StartX=-3 StartY=-73.8 StartZ=0 EndX=-3 EndY=-43.1 EndZ=0
    g14: LineSegment StartX=-3 StartY=-43.1 StartZ=0 EndX=-59.5 EndY=-43.1 EndZ=0
    g15: LineSegment StartX=-59.5 StartY=-43.1 StartZ=0 EndX=-59.5 EndY=-73.8 EndZ=0
  constraints (44):
    c: Coincident(g0,g1)
    c: Coincident(g1,g2)
    c: Coincident(g2,g3)
    c: Coincident(g3,g0)
    c: Vertical(g0)
    c: Vertical(g2)
    c: Horizontal(g1)
    c: Horizontal(g3)
    c: Coincident(g0,g-3)
    c: Coincident(g4,g5)
    c: Coincident(g5,g6)
    c: Coincident(g6,g7)
    c: Coincident(g7,g4)
    c: Horizontal(g4)
    c: Horizontal(g6)
    c: Vertical(g5)
    c: Vertical(g7)
    c: Coincident(g4,g-4)
    c: Coincident(g8,g9)
    c: Coincident(g9,g10)
    c: Coincident(g10,g11)
    c: Coincident(g11,g8)
    c: Vertical(g8)
    c: Vertical(g10)
    c: Horizontal(g9)
    c: Horizontal(g11)
    c: Coincident(g8,g-5)
    c: Coincident(g12,g13)
    c: Coincident(g13,g14)
    c: Coincident(g14,g15)
    c: Coincident(g15,g12)
    c: Horizontal(g12)
    c: Horizontal(g14)
    c: Vertical(g13)
    c: Vertical(g15)
    c: Coincident(g12,g-6)
    c: Vertical(g-9,g12)
    c: Horizontal(g-8,g14)
    c: Horizontal(g-7,g0)
    c: Horizontal(g-13,g6)
    c: Horizontal(g8,g-14)
    c: Vertical(g10,g-10)
    c: Vertical(g4,g-12)
    c: Vertical(g-11,g2)
FEATURE [PartDesign::Pocket] Pocket009
  BaseFeature = -> Pad002
  Direction = (0,0,-1)
  Length = 7.8
  Length2 = 5
  Profile = -> Sketch047
  ReferenceAxis = -> Sketch047 [N_Axis]
  Refine = true
  Suppressed = false
  Type = 0
FEATURE [Sketcher::SketchObject] Sketch048
  ArcFitTolerance = 1e-06
  AttachmentSupport = -> [Pocket009]
  FullyConstrained = true
  MakeInternals = false
  MapMode = 5
  Placement = pos=(0,-75.8,0) rot=(1,0,0;1.5708rad)
  sketch-geometry (2):
    g0: Circle CenterX=-5 CenterY=-6.4 CenterZ=0 NormalX=0 NormalY=0 NormalZ=1 AngleXU=0 Radius=1.2
    g1: Circle CenterX=5 CenterY=-6.4 CenterZ=0 NormalX=0 NormalY=0 NormalZ=1 AngleXU=0 Radius=1.2
  constraints (5):
    c: Symmetric(g0,g1,g-2)
    c: DistanceY(g1,g-1) = 6.4
    c: Equal(g0,g1)
    c: DistanceX(g0,g1) = 10
    c: Radius(g0) = 1.2
FEATURE [PartDesign::Pocket] Pocket010
  BaseFeature = -> Pocket009
  Direction = (0,1,-2e-16)
  Length = 2
  Length2 = 5
  Profile = -> Sketch048
  ReferenceAxis = -> Sketch048 [N_Axis]
  Refine = true
  Suppressed = false
  Type = 0
FEATURE [Sketcher::SketchObject] Sketch049
  ArcFitTolerance = 1e-06
  AttachmentSupport = -> [Pocket006]
  FullyConstrained = true
  MakeInternals = false
  MapMode = 5
  Placement = pos=(29.8,0,0) rot=(0.57735,-0.57735,-0.57735;2.0944rad)
  sketch-geometry (7):
    g0: LineSegment StartX=2.77128 StartY=1.6 StartZ=0 EndX=0 EndY=3.2 EndZ=0
    g1: LineSegment StartX=0 StartY=3.2 StartZ=0 EndX=-2.77128 EndY=1.6 EndZ=0
    g2: LineSegment StartX=-2.77128 StartY=1.6 StartZ=0 EndX=-2.77128 EndY=-1.6 EndZ=0
    g3: LineSegment StartX=-2.77128 StartY=-1.6 StartZ=0 EndX=2.265e-13 EndY=-3.2 EndZ=0
    g4: LineSegment StartX=2.265e-13 StartY=-3.2 StartZ=0 EndX=2.77128 EndY=-1.6 EndZ=0
    g5: LineSegment StartX=2.77128 StartY=-1.6 StartZ=0 EndX=2.77128 EndY=1.6 EndZ=0
    g6: Circle [constr] CenterX=0 CenterY=0 CenterZ=0 NormalX=0 NormalY=0 NormalZ=1 AngleXU=0 Radius=3.2
  constraints (16):
    c: Coincident(g0,g1)
    c: Coincident(g1,g2)
    c: Coincident(g2,g3)
    c: Coincident(g3,g4)
    c: Coincident(g4,g5)
    c: Coincident(g5,g0)
    c: Equal(g0, g1-g5) x5
    c: PointOnObject(g0,g6)
    c: PointOnObject(g1,g6)
    c: PointOnObject(g2,g6)
    c: PointOnObject(g3,g6)
    c: PointOnObject(g4,g6)
    c: PointOnObject(g5,g6)
    c: Coincident(g6,g-1)
    c: PointOnObject(g0,g-2)
    c: Diameter(g6) = 6.4
FEATURE [PartDesign::Pocket] Pocket011
  BaseFeature = -> Pocket006
  Direction = (1,0,0)
  Length = 3
  Length2 = 5
  Profile = -> Sketch049
  ReferenceAxis = -> Sketch049 [N_Axis]
  Refine = true
  Suppressed = false
  Type = 0
FEATURE [Sketcher::SketchObject] Sketch050
  ArcFitTolerance = 1e-06
  AttachmentSupport = -> [Pocket011]
  FullyConstrained = true
  MakeInternals = false
  MapMode = 5
  Placement = pos=(-29.8,0,0) rot=(0.57735,0.57735,0.57735;2.0944rad)
  sketch-geometry (7):
    g0: LineSegment StartX=2.77128 StartY=-1.6 StartZ=0 EndX=2.77128 EndY=1.6 EndZ=0
    g1: LineSegment StartX=2.77128 StartY=1.6 StartZ=0 EndX=0 EndY=3.2 EndZ=0
    g2: LineSegment StartX=0 StartY=3.2 StartZ=0 EndX=-2.77128 EndY=1.6 EndZ=0
    g3: LineSegment StartX=-2.77128 StartY=1.6 StartZ=0 EndX=-2.77128 EndY=-1.6 EndZ=0
    g4: LineSegment StartX=-2.77128 StartY=-1.6 StartZ=0 EndX=0 EndY=-3.2 EndZ=0
    g5: LineSegment StartX=0 StartY=-3.2 StartZ=0 EndX=2.77128 EndY=-1.6 EndZ=0
    g6: Circle [constr] CenterX=0 CenterY=0 CenterZ=0 NormalX=0 NormalY=0 NormalZ=1 AngleXU=0 Radius=3.2
  constraints (16):
    c: Coincident(g0,g1)
    c: Coincident(g1,g2)
    c: Coincident(g2,g3)
    c: Coincident(g3,g4)
    c: Coincident(g4,g5)
    c: Coincident(g5,g0)
    c: Equal(g0, g1-g5) x5
    c: PointOnObject(g0,g6)
    c: PointOnObject(g1,g6)
    c: PointOnObject(g2,g6)
    c: PointOnObject(g3,g6)
    c: PointOnObject(g4,g6)
    c: PointOnObject(g5,g6)
    c: Coincident(g6,g-1)
    c: PointOnObject(g1,g-2)
    c: Diameter(g6) = 6.4
FEATURE [PartDesign::Pocket] Pocket012
  BaseFeature = -> Pocket011
  Direction = (-1,0,0)
  Length = 3
  Length2 = 5
  Profile = -> Sketch050
  ReferenceAxis = -> Sketch050 [N_Axis]
  Refine = true
  Suppressed = false
  Type = 0
FEATURE [Sketcher::SketchObject] Sketch051
  ArcFitTolerance = 1e-06
  AttachmentSupport = -> [Pocket012]
  ExternalGeometry = -> [Pocket012]
  FullyConstrained = true
  MakeInternals = false
  MapMode = 5
  Placement = pos=(0,4,0) rot=(1,0,0;1.5708rad)
  sketch-geometry (12):
    g0: LineSegment StartX=46.7 StartY=0 StartZ=0 EndX=46.7 EndY=-4 EndZ=0
    g1: LineSegment StartX=46.7 StartY=-4 StartZ=0 EndX=61.5 EndY=-4 EndZ=0
    g2: LineSegment StartX=61.5 StartY=-4 StartZ=0 EndX=61.5 EndY=0 EndZ=0
    g3: LineSegment StartX=61.5 StartY=0 StartZ=0 EndX=46.7 EndY=0 EndZ=0
    g4: LineSegment StartX=-29.8 StartY=0 StartZ=0 EndX=-29.8 EndY=-4 EndZ=0
    g5: LineSegment StartX=-29.8 StartY=-4 StartZ=0 EndX=29.8 EndY=-4 EndZ=0
    g6: LineSegment StartX=29.8 StartY=-4 StartZ=0 EndX=29.8 EndY=0 EndZ=0
    g7: LineSegment StartX=29.8 StartY=0 StartZ=0 EndX=-29.8 EndY=0 EndZ=0
    g8: LineSegment StartX=-61.5 StartY=0 StartZ=0 EndX=-61.5 EndY=-4 EndZ=0
    g9: LineSegment StartX=-61.5 StartY=-4 StartZ=0 EndX=-46.7 EndY=-4 EndZ=0
    g10: LineSegment StartX=-46.7 StartY=-4 StartZ=0 EndX=-46.7 EndY=0 EndZ=0
    g11: LineSegment StartX=-46.7 StartY=0 StartZ=0 EndX=-61.5 EndY=0 EndZ=0
  constraints (30):
    c: Coincident(g0,g1)
    c: Coincident(g1,g2)
    c: Coincident(g2,g3)
    c: Coincident(g3,g0)
    c: Vertical(g0)
    c: Vertical(g2)
    c: Horizontal(g1)
    c: Horizontal(g3)
    c: Coincident(g0,g-7)
    c: Coincident(g1,g-8)
    c: Coincident(g4,g5)
    c: Coincident(g5,g6)
    c: Coincident(g6,g7)
    c: Coincident(g7,g4)
    c: Vertical(g4)
    c: Vertical(g6)
    c: Horizontal(g5)
    c: Horizontal(g7)
    c: Coincident(g4,g-5)
    c: Coincident(g5,g-6)
    c: Coincident(g8,g9)
    c: Coincident(g9,g10)
    c: Coincident(g10,g11)
    c: Coincident(g11,g8)
    c: Vertical(g8)
    c: Vertical(g10)
    c: Horizontal(g9)
    c: Horizontal(g11)
    c: Coincident(g8,g-3)
    c: Coincident(g9,g-4)
FEATURE [PartDesign::Pocket] Pocket013
  BaseFeature = -> Pocket012
  Direction = (0,1,-2e-16)
  Length = 0.4
  Length2 = 5
  Profile = -> Sketch051
  ReferenceAxis = -> Sketch051 [N_Axis]
  Refine = true
  Suppressed = false
  Type = 0
FEATURE [PartDesign::Chamfer] Chamfer
  Angle = 45
  Base = -> Pocket013 [Edge56,Edge53,Edge54,Edge55,Edge60,Edge58,Edge57,Edge59]
  BaseFeature = -> Pocket013
  ChamferType = 0
  FlipDirection = false
  Refine = true
  Size = 1
  Size2 = 1
  SupportTransform = false
  Suppressed = false
  UseAllEdges = false
FEATURE [PartDesign::Body] Body001  label="DispHolder"
  AllowCompound = false
  Group = -> [Binder,Sketch035,Pad,Binder003,Sketch038,Pocket001,Binder004,Sketch039,Pocket002,Binder005,Binder006,Binder007,Binder008,Sketch040,Pocket003,Sketch041,Pocket004,Sketch042,Pocket005,Sketch043,Pocket006,Sketch049,Pocket011,Sketch050,Pocket012,Sketch051,Pocket013,Chamfer]
  Origin = -> Origin001
  Tip = -> Chamfer
FEATURE [Sketcher::SketchObject] Sketch052
  ArcFitTolerance = 1e-06
  AttachmentSupport = -> [Pocket010]
  ExternalGeometry = -> [Pocket010]
  FullyConstrained = true
  MakeInternals = false
  MapMode = 5
  Placement = pos=(0,-4,0) rot=(0,0.707107,0.707107;3.14159rad)
  sketch-geometry (8):
    g0: LineSegment StartX=30 StartY=0 StartZ=0 EndX=30 EndY=-4 EndZ=0
    g1: LineSegment StartX=30 StartY=-4 StartZ=0 EndX=46.5 EndY=-4 EndZ=0
    g2: LineSegment StartX=46.5 StartY=-4 StartZ=0 EndX=46.5 EndY=0 EndZ=0
    g3: LineSegment StartX=46.5 StartY=0 StartZ=0 EndX=30 EndY=0 EndZ=0
    g4: LineSegment StartX=-46.5 StartY=0 StartZ=0 EndX=-46.5 EndY=-4 EndZ=0
    g5: LineSegment StartX=-46.5 StartY=-4 StartZ=0 EndX=-30 EndY=-4 EndZ=0
    g6: LineSegment StartX=-30 StartY=-4 StartZ=0 EndX=-30 EndY=0 EndZ=0
    g7: LineSegment StartX=-30 StartY=0 StartZ=0 EndX=-46.5 EndY=0 EndZ=0
  constraints (20):
    c: Coincident(g0,g1)
    c: Coincident(g1,g2)
    c: Coincident(g2,g3)
    c: Coincident(g3,g0)
    c: Vertical(g0)
    c: Vertical(g2)
    c: Horizontal(g1)
    c: Horizontal(g3)
    c: Coincident(g0,g-5)
    c: Coincident(g1,g-6)
    c: Coincident(g4,g5)
    c: Coincident(g5,g6)
    c: Coincident(g6,g7)
    c: Coincident(g7,g4)
    c: Vertical(g4)
    c: Vertical(g6)
    c: Horizontal(g5)
    c: Horizontal(g7)
    c: Coincident(g4,g-3)
    c: Coincident(g5,g-4)
FEATURE [PartDesign::Pocket] Pocket014
  BaseFeature = -> Pocket010
  Direction = (0,-1,2e-16)
  Length = 0.4
  Length2 = 5
  Profile = -> Sketch052
  ReferenceAxis = -> Sketch052 [N_Axis]
  Refine = true
  Suppressed = false
  Type = 0
FEATURE [PartDesign::SubShapeBinder] Binder011
  BindCopyOnChange = 0
  BindMode = 0
  ClaimChildren = false
  Context = -> Body002 [Binder011.]
  Fuse = false
  MakeFace = true
  OffsetFill = false
  OffsetIntersection = false
  OffsetJoinType = 0
  OffsetOpenResult = false
  PartialLoad = false
  Refine = true
  Relative = true
  Support = -> [Body[Sketch032.Edge19,Sketch032.Edge20,Sketch032.Edge17,Sketch032.Edge18,Sketch032.Edge28,Sketch032.Edge25,Sketch032.Edge26,Sketch032.Edge27]]
  _Version = 2
FEATURE [Sketcher::SketchObject] Sketch053
  ArcFitTolerance = 1e-06
  AttachmentSupport = -> [Pocket014]
  ExternalGeometry = -> [Binder011]
  FullyConstrained = true
  MakeInternals = false
  MapMode = 5
  Placement = pos=(0,-4.4,0) rot=(0,0.707107,0.707107;3.14159rad)
  sketch-geometry (4):
    g0: LineSegment StartX=-35.3 StartY=-2.3 StartZ=0 EndX=-35.3 EndY=-7.8 EndZ=0
    g1: LineSegment StartX=-35.3 StartY=-7.8 StartZ=0 EndX=-20.9 EndY=-7.8 EndZ=0
    g2: LineSegment StartX=-20.9 StartY=-7.8 StartZ=0 EndX=-20.9 EndY=-2.3 EndZ=0
    g3: LineSegment StartX=-20.9 StartY=-2.3 StartZ=0 EndX=-35.3 EndY=-2.3 EndZ=0
  constraints (12):
    c: Coincident(g0,g1)
    c: Coincident(g1,g2)
    c: Coincident(g2,g3)
    c: Coincident(g3,g0)
    c: Vertical(g0)
    c: Vertical(g2)
    c: Horizontal(g1)
    c: Horizontal(g3)
    c: DistanceY(g0,g0) = 5.5
    c: DistanceX(g0,g-3) = 1
    c: DistanceX(g-3,g2) = 1
    c: DistanceY(g2,g-3) = 2.3
FEATURE [PartDesign::Pocket] Pocket015
  BaseFeature = -> Pocket014
  Direction = (0,-1,2e-16)
  Length = 2.2
  Length2 = 5
  Profile = -> Sketch053
  ReferenceAxis = -> Sketch053 [N_Axis]
  Refine = true
  Suppressed = false
  Type = 0
FEATURE [Sketcher::SketchObject] Sketch054
  ArcFitTolerance = 1e-06
  AttachmentSupport = -> [Pocket015]
  ExternalGeometry = -> [Binder011]
  FullyConstrained = true
  MakeInternals = false
  MapMode = 5
  Placement = pos=(61.5,0,0) rot=(0.57735,0.57735,0.57735;2.0944rad)
  sketch-geometry (4):
    g0: LineSegment StartX=-66.2 StartY=-2 StartZ=0 EndX=-66.2 EndY=-8 EndZ=0
    g1: LineSegment StartX=-66.2 StartY=-8 StartZ=0 EndX=-52.2 EndY=-8 EndZ=0
    g2: LineSegment StartX=-52.2 StartY=-8 StartZ=0 EndX=-52.2 EndY=-2 EndZ=0
    g3: LineSegment StartX=-52.2 StartY=-2 StartZ=0 EndX=-66.2 EndY=-2 EndZ=0
  constraints (12):
    c: Coincident(g0,g1)
    c: Coincident(g1,g2)
    c: Coincident(g2,g3)
    c: Coincident(g3,g0)
    c: Vertical(g0)
    c: Vertical(g2)
    c: Horizontal(g1)
    c: Horizontal(g3)
    c: DistanceX(g1,g1) = 14
    c: DistanceY(g2,g2) = 6
    c: DistanceX(g2,g-3) = 5
    c: DistanceY(g0,g-3) = 2
FEATURE [PartDesign::Pocket] Pocket016
  BaseFeature = -> Pocket015
  Direction = (-1,0,0)
  Length = 2
  Length2 = 5
  Profile = -> Sketch054
  ReferenceAxis = -> Sketch054 [N_Axis]
  Refine = true
  Suppressed = false
  Type = 0
FEATURE [Sketcher::SketchObject] Sketch055
  ArcFitTolerance = 1e-06
  AttachmentSupport = -> [Pocket016]
  FullyConstrained = true
  MakeInternals = false
  MapMode = 5
  Placement = pos=(61.5,0,0) rot=(0.57735,0.57735,0.57735;2.0944rad)
  sketch-geometry (1):
    g0: Circle CenterX=0 CenterY=0 CenterZ=0 NormalX=0 NormalY=0 NormalZ=1 AngleXU=0 Radius=3
  constraints (2):
    c: Coincident(g0,g-1)
    c: Radius(g0) = 3
FEATURE [PartDesign::Pocket] Pocket017
  BaseFeature = -> Pocket016
  Direction = (-1,0,0)
  Length = 4
  Length2 = 5
  Profile = -> Sketch055
  ReferenceAxis = -> Sketch055 [N_Axis]
  Refine = true
  Suppressed = false
  Type = 0
FEATURE [Sketcher::SketchObject] Sketch056
  ArcFitTolerance = 1e-06
  AttachmentSupport = -> [Pocket017]
  FullyConstrained = true
  MakeInternals = false
  MapMode = 5
  Placement = pos=(-61.5,0,0) rot=(0.57735,-0.57735,-0.57735;2.0944rad)
  sketch-geometry (1):
    g0: Circle CenterX=0 CenterY=0 CenterZ=0 NormalX=0 NormalY=0 NormalZ=1 AngleXU=0 Radius=3
  constraints (2):
    c: Coincident(g0,g-1)
    c: Radius(g0) = 3
FEATURE [PartDesign::Pocket] Pocket018
  BaseFeature = -> Pocket017
  Direction = (1,0,0)
  Length = 4
  Length2 = 5
  Profile = -> Sketch056
  ReferenceAxis = -> Sketch056 [N_Axis]
  Refine = true
  Suppressed = false
  Type = 0
FEATURE [PartDesign::Body] Body002  label="MainHolder"
  AllowCompound = false
  Group = -> [Binder001,Sketch036,Pad001,Binder002,Sketch037,Pocket,Binder009,Binder010,Sketch044,Pocket007,Sketch045,Pocket008,Sketch046,Pad002,Sketch047,Pocket009,Sketch048,Pocket010,Sketch052,Pocket014,Binder011,Sketch053,Pocket015,Sketch054,Pocket016,Sketch055,Pocket017,Sketch056,Pocket018]
  Origin = -> Origin002
  Tip = -> Pocket018
FEATURE [Mesh::Feature] Mesh  label="Chamfer (Meshed)"
  Placement = pos=(0,0,0) rot=(1,0,0;0.523599rad)
FEATURE [Mesh::Feature] Mesh001  label="Pocket018 (Meshed)"
